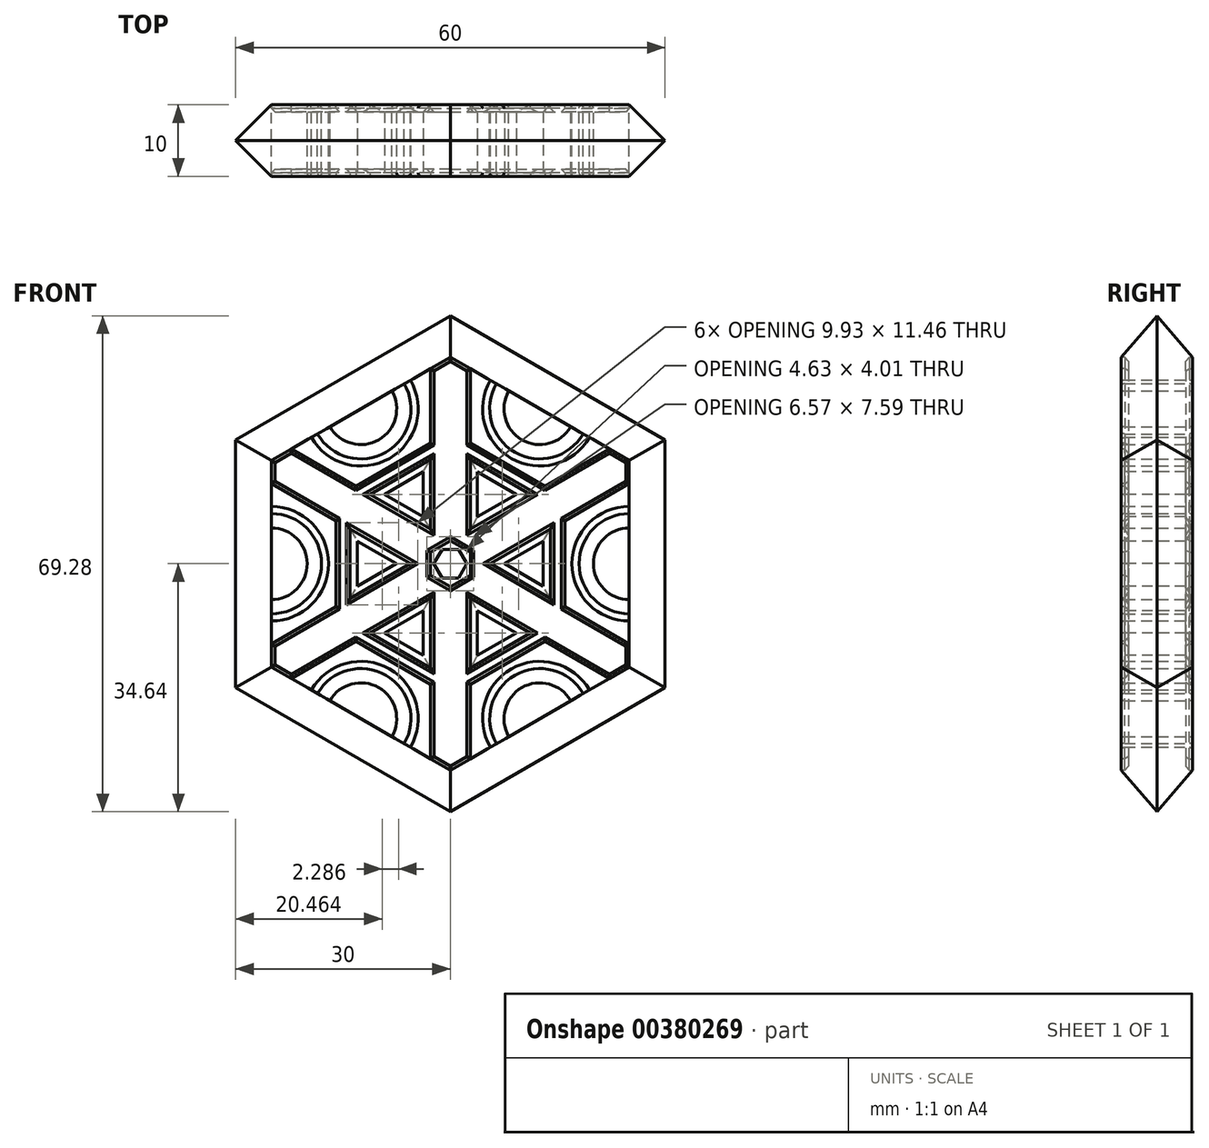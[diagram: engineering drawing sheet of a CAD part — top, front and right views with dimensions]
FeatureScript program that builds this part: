
annotation { "Feature Type Name" : "Feature", "Feature Type Description" : "" }
export const myFeature = defineFeature(function(context is Context, id is Id, definition is map)
    precondition{}
    {
        {
            var Q0;
            Q0=qCreatedBy(makeId("Front.planeOp"),FACE);
            var sketch = newSketch(context, id + "F0", { "sketchPlane" : qUnion([Q0])});
            skCircle(sketch, "E0.cCircle", {"center": v(0, 0) * mm, "radius": 25 * mm, "construction": true});
            skLineSegment(sketch, "E0.0", {"start": v(-25, -14.43) * mm, "end": v(-25, 14.43) * mm});
            skLineSegment(sketch, "E0.1", {"start": v(-25, 14.43) * mm, "end": v(0, 28.87) * mm});
            skLineSegment(sketch, "E0.2", {"start": v(0, 28.87) * mm, "end": v(25, 14.43) * mm});
            skLineSegment(sketch, "E0.3", {"start": v(25, 14.43) * mm, "end": v(25, -14.43) * mm});
            skLineSegment(sketch, "E0.4", {"start": v(25, -14.43) * mm, "end": v(0, -28.87) * mm});
            skLineSegment(sketch, "E0.5", {"start": v(0, -28.87) * mm, "end": v(-25, -14.43) * mm});
            skPoint(sketch, "E0.0.midPoint", {"position": v(-25, 0) * mm});
            skCircle(sketch, "E1", {"center": v(-12.5, 21.65) * mm, "radius": 5 * mm});
            skCircle(sketch, "E2", {"center": v(12.5, 21.65) * mm, "radius": 5 * mm});
            skCircle(sketch, "E3", {"center": v(25, 0) * mm, "radius": 5 * mm});
            skCircle(sketch, "E4", {"center": v(12.5, -21.65) * mm, "radius": 5 * mm});
            skCircle(sketch, "E5", {"center": v(-12.5, -21.65) * mm, "radius": 5 * mm});
            skCircle(sketch, "E6", {"center": v(-25, 0) * mm, "radius": 5 * mm});
            skArc(sketch, "E7", {"start": v(-25, -7) * mm, "mid": v(-18, 0) * mm, "end": v(-25, 7) * mm});
            skArc(sketch, "E8", {"start": v(-6.44, -25.15) * mm, "mid": v(-9, -15.59) * mm, "end": v(-18.56, -18.15) * mm});
            skArc(sketch, "E9", {"start": v(18.56, -18.15) * mm, "mid": v(9, -15.59) * mm, "end": v(6.44, -25.15) * mm});
            skCircle(sketch, "E10.cCircle", {"center": v(0, 0) * mm, "radius": 30 * mm, "construction": true});
            skLineSegment(sketch, "E10.0", {"start": v(-30, -17.32) * mm, "end": v(-30, 17.32) * mm});
            skLineSegment(sketch, "E10.1", {"start": v(-30, 17.32) * mm, "end": v(0, 34.64) * mm});
            skLineSegment(sketch, "E10.2", {"start": v(0, 34.64) * mm, "end": v(30, 17.32) * mm});
            skLineSegment(sketch, "E10.3", {"start": v(30, 17.32) * mm, "end": v(30, -17.32) * mm});
            skLineSegment(sketch, "E10.4", {"start": v(30, -17.32) * mm, "end": v(0, -34.64) * mm});
            skLineSegment(sketch, "E10.5", {"start": v(0, -34.64) * mm, "end": v(-30, -17.32) * mm});
            skPoint(sketch, "E10.0.midPoint", {"position": v(-30, 0) * mm});
            skArc(sketch, "E11", {"start": v(6.44, 25.15) * mm, "mid": v(9, 15.59) * mm, "end": v(18.56, 18.15) * mm});
            skArc(sketch, "E12", {"start": v(25, 7) * mm, "mid": v(18, 0) * mm, "end": v(25, -7) * mm});
            skArc(sketch, "E13", {"start": v(-18.56, 18.15) * mm, "mid": v(-9, 15.59) * mm, "end": v(-6.44, 25.15) * mm});
            skArc(sketch, "E14", {"start": v(-25, -8) * mm, "mid": v(-17, 0) * mm, "end": v(-25, 8) * mm});
            skArc(sketch, "E15", {"start": v(-19.43, 17.65) * mm, "mid": v(-8.5, 14.72) * mm, "end": v(-5.57, 25.65) * mm});
            skArc(sketch, "E16", {"start": v(5.57, 25.65) * mm, "mid": v(8.5, 14.72) * mm, "end": v(19.43, 17.65) * mm});
            skArc(sketch, "E17", {"start": v(25, 8) * mm, "mid": v(17, 0) * mm, "end": v(25, -8) * mm});
            skArc(sketch, "E18", {"start": v(19.43, -17.65) * mm, "mid": v(8.5, -14.72) * mm, "end": v(5.57, -25.65) * mm});
            skArc(sketch, "E19", {"start": v(-5.57, -25.65) * mm, "mid": v(-8.5, -14.72) * mm, "end": v(-19.43, -17.65) * mm});
            skSolve(sketch);
        }
        {
            var Q0;
            {var subQ0=sQuery(id+"F0.wireOp",EDGE,"E6");var subQ1=sQuery(id+"F0.wireOp",EDGE,"E0.0");var subQ2=makeQuery(id+"F0.imprint","INTERSECT",VERTEX,{"disambiguationData":[OD(0.0)],"derivedFrom":[subQ1,subQ0]});Q0=makeQuery(id+"F0.imprint","IMPRINT",FACE,{"disambiguationData":[TD([[makeQuery(id+"F0.imprint","IMPRINT",EDGE,{"disambiguationData":[TD([[subQ2,-1.0]])],"derivedFrom":subQ1}),1.0]])]});}
            var Q1;
            {var subQ0=sQuery(id+"F0.wireOp",EDGE,"E2");var subQ1=sQuery(id+"F0.wireOp",EDGE,"E0.2");var subQ2=makeQuery(id+"F0.imprint","INTERSECT",VERTEX,{"disambiguationData":[OD(0.0)],"derivedFrom":[subQ1,subQ0]});Q1=makeQuery(id+"F0.imprint","IMPRINT",FACE,{"disambiguationData":[TD([[makeQuery(id+"F0.imprint","IMPRINT",EDGE,{"disambiguationData":[TD([[subQ2,-1.0]])],"derivedFrom":subQ1}),1.0]])]});}
            var Q2;
            {var subQ0=sQuery(id+"F0.wireOp",EDGE,"E3");var subQ1=sQuery(id+"F0.wireOp",EDGE,"E0.3");var subQ2=makeQuery(id+"F0.imprint","INTERSECT",VERTEX,{"disambiguationData":[OD(0.0)],"derivedFrom":[subQ1,subQ0]});Q2=makeQuery(id+"F0.imprint","IMPRINT",FACE,{"disambiguationData":[TD([[makeQuery(id+"F0.imprint","IMPRINT",EDGE,{"disambiguationData":[TD([[subQ2,-1.0]])],"derivedFrom":subQ1}),1.0]])]});}
            var Q3;
            {var subQ0=sQuery(id+"F0.wireOp",EDGE,"E4");var subQ1=sQuery(id+"F0.wireOp",EDGE,"E0.4");var subQ2=makeQuery(id+"F0.imprint","INTERSECT",VERTEX,{"disambiguationData":[OD(0.0)],"derivedFrom":[subQ1,subQ0]});Q3=makeQuery(id+"F0.imprint","IMPRINT",FACE,{"disambiguationData":[TD([[makeQuery(id+"F0.imprint","IMPRINT",EDGE,{"disambiguationData":[TD([[subQ2,-1.0]])],"derivedFrom":subQ1}),1.0]])]});}
            var Q4;
            {var subQ0=sQuery(id+"F0.wireOp",EDGE,"E5");var subQ1=sQuery(id+"F0.wireOp",EDGE,"E0.5");var subQ2=makeQuery(id+"F0.imprint","INTERSECT",VERTEX,{"disambiguationData":[OD(0.0)],"derivedFrom":[subQ1,subQ0]});Q4=makeQuery(id+"F0.imprint","IMPRINT",FACE,{"disambiguationData":[TD([[makeQuery(id+"F0.imprint","IMPRINT",EDGE,{"disambiguationData":[TD([[subQ2,-1.0]])],"derivedFrom":subQ1}),1.0]])]});}
            var Q5;
            {var subQ0=sQuery(id+"F0.wireOp",EDGE,"E0.5");var subQ1=sQuery(id+"F0.wireOp",EDGE,"E0.0");var subQ2=makeQuery(id+"F0.imprint","INTERSECT",VERTEX,{"derivedFrom":[subQ1,subQ0]});Q5=makeQuery(id+"F0.imprint","IMPRINT",FACE,{"disambiguationData":[TD([[makeQuery(id+"F0.imprint","IMPRINT",EDGE,{"disambiguationData":[TD([[subQ2,-1.0]])],"derivedFrom":subQ1}),1.0]])]});}
            var Q6;
            {var subQ4=sQuery(id+"F0.wireOp",EDGE,"E0.0");var subQ6=makeQuery(id+"F0.imprint","INTERSECT",VERTEX,{"disambiguationData":[OD(1.0)],"derivedFrom":[subQ4,sQuery(id+"F0.wireOp",EDGE,"E7")]});Q6=makeQuery(id+"F0.imprint","IMPRINT",FACE,{"disambiguationData":[TD([[makeQuery(id+"F0.imprint","IMPRINT",EDGE,{"disambiguationData":[TD([[subQ6,1.0]])],"derivedFrom":subQ4}),1.0]])]});}
            var Q7;
            {var subQ8=sQuery(id+"F0.wireOp",EDGE,"E0.1");var subQ12=makeQuery(id+"F0.imprint","INTERSECT",VERTEX,{"disambiguationData":[OD(1.0)],"derivedFrom":[subQ8,sQuery(id+"F0.wireOp",EDGE,"E13")]});Q7=makeQuery(id+"F0.imprint","IMPRINT",FACE,{"disambiguationData":[TD([[makeQuery(id+"F0.imprint","IMPRINT",EDGE,{"disambiguationData":[TD([[subQ12,1.0]])],"derivedFrom":subQ8}),1.0]])]});}
            var Q8;
            {var subQ4=sQuery(id+"F0.wireOp",EDGE,"E0.2");var subQ6=makeQuery(id+"F0.imprint","INTERSECT",VERTEX,{"disambiguationData":[OD(1.0)],"derivedFrom":[subQ4,sQuery(id+"F0.wireOp",EDGE,"E11")]});Q8=makeQuery(id+"F0.imprint","IMPRINT",FACE,{"disambiguationData":[TD([[makeQuery(id+"F0.imprint","IMPRINT",EDGE,{"disambiguationData":[TD([[subQ6,1.0]])],"derivedFrom":subQ4}),1.0]])]});}
            var Q9;
            {var subQ4=sQuery(id+"F0.wireOp",EDGE,"E0.3");var subQ6=makeQuery(id+"F0.imprint","INTERSECT",VERTEX,{"disambiguationData":[OD(1.0)],"derivedFrom":[subQ4,sQuery(id+"F0.wireOp",EDGE,"E12")]});Q9=makeQuery(id+"F0.imprint","IMPRINT",FACE,{"disambiguationData":[TD([[makeQuery(id+"F0.imprint","IMPRINT",EDGE,{"disambiguationData":[TD([[subQ6,1.0]])],"derivedFrom":subQ4}),1.0]])]});}
            var Q10;
            {var subQ4=sQuery(id+"F0.wireOp",EDGE,"E0.4");var subQ6=makeQuery(id+"F0.imprint","INTERSECT",VERTEX,{"disambiguationData":[OD(1.0)],"derivedFrom":[subQ4,sQuery(id+"F0.wireOp",EDGE,"E9")]});Q10=makeQuery(id+"F0.imprint","IMPRINT",FACE,{"disambiguationData":[TD([[makeQuery(id+"F0.imprint","IMPRINT",EDGE,{"disambiguationData":[TD([[subQ6,1.0]])],"derivedFrom":subQ4}),1.0]])]});}
            var Q11;
            {var subQ0=sQuery(id+"F0.wireOp",EDGE,"E1");var subQ1=sQuery(id+"F0.wireOp",EDGE,"E0.1");var subQ2=makeQuery(id+"F0.imprint","INTERSECT",VERTEX,{"disambiguationData":[OD(0.0)],"derivedFrom":[subQ1,subQ0]});Q11=makeQuery(id+"F0.imprint","IMPRINT",FACE,{"disambiguationData":[TD([[makeQuery(id+"F0.imprint","IMPRINT",EDGE,{"disambiguationData":[TD([[subQ2,-1.0]])],"derivedFrom":subQ1}),1.0]])]});}
            var Q12;
            {var subQ15=sQuery(id+"F0.wireOp",EDGE,"E14");Q12=makeQuery(id+"F0.imprint","IMPRINT",FACE,{"disambiguationData":[TD([[makeQuery(id+"F0.imprint","IMPRINT",EDGE,{"derivedFrom":subQ15}),-1.0]])]});}
            var Q13;
            {var subQ0=sQuery(id+"F0.wireOp",EDGE,"E7");Q13=makeQuery(id+"F0.imprint","IMPRINT",FACE,{"disambiguationData":[TD([[makeQuery(id+"F0.imprint","IMPRINT",EDGE,{"derivedFrom":subQ0}),1.0]])]});}
            var Q14;
            {var subQ0=sQuery(id+"F0.wireOp",EDGE,"E13");Q14=makeQuery(id+"F0.imprint","IMPRINT",FACE,{"disambiguationData":[TD([[makeQuery(id+"F0.imprint","IMPRINT",EDGE,{"derivedFrom":subQ0}),1.0]])]});}
            var Q15;
            {var subQ0=sQuery(id+"F0.wireOp",EDGE,"E11");Q15=makeQuery(id+"F0.imprint","IMPRINT",FACE,{"disambiguationData":[TD([[makeQuery(id+"F0.imprint","IMPRINT",EDGE,{"derivedFrom":subQ0}),1.0]])]});}
            var Q16;
            {var subQ0=sQuery(id+"F0.wireOp",EDGE,"E12");Q16=makeQuery(id+"F0.imprint","IMPRINT",FACE,{"disambiguationData":[TD([[makeQuery(id+"F0.imprint","IMPRINT",EDGE,{"derivedFrom":subQ0}),1.0]])]});}
            var Q17;
            {var subQ0=sQuery(id+"F0.wireOp",EDGE,"E9");Q17=makeQuery(id+"F0.imprint","IMPRINT",FACE,{"disambiguationData":[TD([[makeQuery(id+"F0.imprint","IMPRINT",EDGE,{"derivedFrom":subQ0}),1.0]])]});}
            var Q18;
            {var subQ0=sQuery(id+"F0.wireOp",EDGE,"E8");Q18=makeQuery(id+"F0.imprint","IMPRINT",FACE,{"disambiguationData":[TD([[makeQuery(id+"F0.imprint","IMPRINT",EDGE,{"derivedFrom":subQ0}),1.0]])]});}
            extrude(context, id + "F1", {"entities" : qUnion([Q0, Q1, Q2, Q3, Q4, Q5, Q6, Q7, Q8, Q9, Q10, Q11, Q12, Q13, Q14, Q15, Q16, Q17, Q18]), "depth" : 10 * mm});
        }
        {
            var Q0;
            Q0=makeQuery(id+"F1.opExtrude","CAP_EDGE",EDGE,{"disambiguationData":[OSD([sQuery(id+"F0.wireOp",EDGE,"E10.0")])],"isStart":false});
            var Q1;
            Q1=makeQuery(id+"F1.opExtrude","CAP_EDGE",EDGE,{"disambiguationData":[OSD([sQuery(id+"F0.wireOp",EDGE,"E10.1")])],"isStart":false});
            var Q2;
            Q2=makeQuery(id+"F1.opExtrude","CAP_EDGE",EDGE,{"disambiguationData":[OSD([sQuery(id+"F0.wireOp",EDGE,"E10.2")])],"isStart":false});
            var Q3;
            Q3=makeQuery(id+"F1.opExtrude","CAP_EDGE",EDGE,{"disambiguationData":[OSD([sQuery(id+"F0.wireOp",EDGE,"E10.3")])],"isStart":false});
            var Q4;
            Q4=makeQuery(id+"F1.opExtrude","CAP_EDGE",EDGE,{"disambiguationData":[OSD([sQuery(id+"F0.wireOp",EDGE,"E10.4")])],"isStart":false});
            var Q5;
            Q5=makeQuery(id+"F1.opExtrude","CAP_EDGE",EDGE,{"disambiguationData":[OSD([sQuery(id+"F0.wireOp",EDGE,"E10.5")])],"isStart":false});
            var Q6;
            Q6=makeQuery(id+"F1.opExtrude","CAP_EDGE",EDGE,{"disambiguationData":[OSD([sQuery(id+"F0.wireOp",EDGE,"E10.3")])],"isStart":true});
            var Q7;
            Q7=makeQuery(id+"F1.opExtrude","CAP_EDGE",EDGE,{"disambiguationData":[OSD([sQuery(id+"F0.wireOp",EDGE,"E10.2")])],"isStart":true});
            var Q8;
            Q8=makeQuery(id+"F1.opExtrude","CAP_EDGE",EDGE,{"disambiguationData":[OSD([sQuery(id+"F0.wireOp",EDGE,"E10.1")])],"isStart":true});
            var Q9;
            Q9=makeQuery(id+"F1.opExtrude","CAP_EDGE",EDGE,{"disambiguationData":[OSD([sQuery(id+"F0.wireOp",EDGE,"E10.0")])],"isStart":true});
            var Q10;
            Q10=makeQuery(id+"F1.opExtrude","CAP_EDGE",EDGE,{"disambiguationData":[OSD([sQuery(id+"F0.wireOp",EDGE,"E10.5")])],"isStart":true});
            var Q11;
            Q11=makeQuery(id+"F1.opExtrude","CAP_EDGE",EDGE,{"disambiguationData":[OSD([sQuery(id+"F0.wireOp",EDGE,"E10.4")])],"isStart":true});
            chamfer(context, id + "F2", {"entities" : qUnion([Q0, Q1, Q2, Q3, Q4, Q5, Q6, Q7, Q8, Q9, Q10, Q11]), "width" : 5 * mm, "tangentPropagation" : true});
        }
        {
            var Q0;
            Q0=makeQuery(id+"F2.opChamfer","SPLIT",FACE,{"disambiguationData":[OD(6.0)],"derivedFrom":makeQuery(id+"F1.opExtrude","CAP_FACE",FACE,{"disambiguationData":[OSD([sQuery(id+"F0.wireOp",EDGE,"E0.0"),sQuery(id+"F0.wireOp",EDGE,"E0.1"),sQuery(id+"F0.wireOp",EDGE,"E0.2"),sQuery(id+"F0.wireOp",EDGE,"E0.3"),sQuery(id+"F0.wireOp",EDGE,"E0.4"),sQuery(id+"F0.wireOp",EDGE,"E0.5"),sQuery(id+"F0.wireOp",EDGE,"E1"),sQuery(id+"F0.wireOp",EDGE,"E2"),sQuery(id+"F0.wireOp",EDGE,"E3"),sQuery(id+"F0.wireOp",EDGE,"E4"),sQuery(id+"F0.wireOp",EDGE,"E5"),sQuery(id+"F0.wireOp",EDGE,"E6"),sQuery(id+"F0.wireOp",EDGE,"E7"),sQuery(id+"F0.wireOp",EDGE,"E8"),sQuery(id+"F0.wireOp",EDGE,"E9"),sQuery(id+"F0.wireOp",EDGE,"E10.0"),sQuery(id+"F0.wireOp",EDGE,"E10.1"),sQuery(id+"F0.wireOp",EDGE,"E10.2"),sQuery(id+"F0.wireOp",EDGE,"E10.3"),sQuery(id+"F0.wireOp",EDGE,"E10.4"),sQuery(id+"F0.wireOp",EDGE,"E10.5"),sQuery(id+"F0.wireOp",EDGE,"E11"),sQuery(id+"F0.wireOp",EDGE,"E12"),sQuery(id+"F0.wireOp",EDGE,"E13"),sQuery(id+"F0.wireOp",EDGE,"E14"),sQuery(id+"F0.wireOp",EDGE,"E15"),sQuery(id+"F0.wireOp",EDGE,"E16"),sQuery(id+"F0.wireOp",EDGE,"E17"),sQuery(id+"F0.wireOp",EDGE,"E18"),sQuery(id+"F0.wireOp",EDGE,"E19")])],"isStart":false})});
            var sketch = newSketch(context, id + "F3", { "sketchPlane" : qUnion([Q0])});
            skLineSegment(sketch, "E20", {"start": v(-25, -11.22) * mm, "end": v(22.21, 16.04) * mm});
            skLineSegment(sketch, "E21", {"start": v(-22.21, -16.04) * mm, "end": v(25, 11.22) * mm});
            skLineSegment(sketch, "E22", {"start": v(-2.79, 27.26) * mm, "end": v(-2.79, -27.26) * mm});
            skLineSegment(sketch, "E23", {"start": v(2.79, 27.26) * mm, "end": v(2.79, -27.26) * mm});
            skLineSegment(sketch, "E24", {"start": v(-25, 11.22) * mm, "end": v(22.21, -16.04) * mm});
            skLineSegment(sketch, "E25", {"start": v(-22.21, 16.04) * mm, "end": v(25, -11.22) * mm});
            skLineSegment(sketch, "E26", {"start": v(-25, 14.43) * mm, "end": v(-22.21, 16.04) * mm});
            skLineSegment(sketch, "E27", {"start": v(-25, 14.43) * mm, "end": v(-25, 11.22) * mm});
            skLineSegment(sketch, "E28", {"start": v(-2.79, 27.26) * mm, "end": v(0, 28.87) * mm});
            skLineSegment(sketch, "E29", {"start": v(0, 28.87) * mm, "end": v(2.79, 27.26) * mm});
            skLineSegment(sketch, "E30", {"start": v(22.21, 16.04) * mm, "end": v(25, 14.43) * mm});
            skLineSegment(sketch, "E31", {"start": v(25, 14.43) * mm, "end": v(25, 11.22) * mm});
            skLineSegment(sketch, "E32", {"start": v(25, -11.22) * mm, "end": v(25, -14.43) * mm});
            skLineSegment(sketch, "E33", {"start": v(25, -14.43) * mm, "end": v(22.21, -16.04) * mm});
            skLineSegment(sketch, "E34", {"start": v(2.79, -27.26) * mm, "end": v(0, -28.87) * mm});
            skLineSegment(sketch, "E35", {"start": v(0, -28.87) * mm, "end": v(-2.79, -27.26) * mm});
            skLineSegment(sketch, "E36", {"start": v(-22.21, -16.04) * mm, "end": v(-25, -14.43) * mm});
            skLineSegment(sketch, "E37", {"start": v(-25, -14.43) * mm, "end": v(-25, -11.22) * mm});
            skCircle(sketch, "E38.cCircle", {"center": v(0, 0) * mm, "radius": 16 * mm, "construction": true});
            skLineSegment(sketch, "E38.0", {"start": v(-16, -9.24) * mm, "end": v(-16, 9.24) * mm});
            skLineSegment(sketch, "E38.1", {"start": v(-16, 9.24) * mm, "end": v(0, 18.48) * mm});
            skLineSegment(sketch, "E38.2", {"start": v(0, 18.48) * mm, "end": v(16, 9.24) * mm});
            skLineSegment(sketch, "E38.3", {"start": v(16, 9.24) * mm, "end": v(16, -9.24) * mm});
            skLineSegment(sketch, "E38.4", {"start": v(16, -9.24) * mm, "end": v(0, -18.48) * mm});
            skLineSegment(sketch, "E38.5", {"start": v(0, -18.48) * mm, "end": v(-16, -9.24) * mm});
            skPoint(sketch, "E38.0.midPoint", {"position": v(-16, 0) * mm});
            skCircle(sketch, "E39.cCircle", {"center": v(0, 0) * mm, "radius": 14 * mm, "construction": true});
            skPoint(sketch, "E39.cCircle.perimeterSnap0", {"position": v(-2.79, 0) * mm});
            skLineSegment(sketch, "E39.0", {"start": v(-14, -8.08) * mm, "end": v(-14, 8.08) * mm});
            skLineSegment(sketch, "E39.1", {"start": v(-14, 8.08) * mm, "end": v(0, 16.17) * mm});
            skLineSegment(sketch, "E39.2", {"start": v(0, 16.17) * mm, "end": v(14, 8.08) * mm});
            skLineSegment(sketch, "E39.3", {"start": v(14, 8.08) * mm, "end": v(14, -8.08) * mm});
            skLineSegment(sketch, "E39.4", {"start": v(14, -8.08) * mm, "end": v(0, -16.17) * mm});
            skLineSegment(sketch, "E39.5", {"start": v(0, -16.17) * mm, "end": v(-14, -8.08) * mm});
            skPoint(sketch, "E39.0.midPoint", {"position": v(-14, 0) * mm});
            skPoint(sketch, "E39.0.midPoint.positionSnap0", {"position": v(-2.79, 0) * mm});
            skSolve(sketch);
        }
        {
            var Q0;
            {var subQ7=sQuery(id+"F3.wireOp",EDGE,"E36");Q0=makeQuery(id+"F3.imprint","IMPRINT",FACE,{"disambiguationData":[TD([[makeQuery(id+"F3.imprint","IMPRINT",EDGE,{"derivedFrom":subQ7}),1.0]])]});}
            var Q1;
            {var subQ0=sQuery(id+"F3.wireOp",EDGE,"E26");Q1=makeQuery(id+"F3.imprint","IMPRINT",FACE,{"disambiguationData":[TD([[makeQuery(id+"F3.imprint","IMPRINT",EDGE,{"derivedFrom":subQ0}),1.0]])]});}
            var Q2;
            {var subQ11=sQuery(id+"F3.wireOp",EDGE,"E28");Q2=makeQuery(id+"F3.imprint","IMPRINT",FACE,{"disambiguationData":[TD([[makeQuery(id+"F3.imprint","IMPRINT",EDGE,{"derivedFrom":subQ11}),1.0]])]});}
            var Q3;
            {var subQ11=sQuery(id+"F3.wireOp",EDGE,"E30");Q3=makeQuery(id+"F3.imprint","IMPRINT",FACE,{"disambiguationData":[TD([[makeQuery(id+"F3.imprint","IMPRINT",EDGE,{"derivedFrom":subQ11}),1.0]])]});}
            var Q4;
            {var subQ5=sQuery(id+"F3.wireOp",EDGE,"E34");Q4=makeQuery(id+"F3.imprint","IMPRINT",FACE,{"disambiguationData":[TD([[makeQuery(id+"F3.imprint","IMPRINT",EDGE,{"derivedFrom":subQ5}),1.0]])]});}
            var Q5;
            {var subQ0=sQuery(id+"F3.wireOp",EDGE,"E32");Q5=makeQuery(id+"F3.imprint","IMPRINT",FACE,{"disambiguationData":[TD([[makeQuery(id+"F3.imprint","IMPRINT",EDGE,{"derivedFrom":subQ0}),1.0]])]});}
            var Q6;
            {var subQ0=sQuery(id+"F3.wireOp",EDGE,"E22");var subQ1=sQuery(id+"F3.wireOp",EDGE,"E20");var subQ2=makeQuery(id+"F3.imprint","INTERSECT",VERTEX,{"derivedFrom":[subQ1,subQ0]});Q6=makeQuery(id+"F3.imprint","IMPRINT",FACE,{"disambiguationData":[TD([[makeQuery(id+"F3.imprint","IMPRINT",EDGE,{"disambiguationData":[TD([[subQ2,-1.0]])],"derivedFrom":subQ1}),1.0]])]});}
            var Q7;
            {var subQ0=sQuery(id+"F3.wireOp",EDGE,"E25");var subQ1=sQuery(id+"F3.wireOp",EDGE,"E20");var subQ2=makeQuery(id+"F3.imprint","INTERSECT",VERTEX,{"derivedFrom":[subQ1,subQ0]});Q7=makeQuery(id+"F3.imprint","IMPRINT",FACE,{"disambiguationData":[TD([[makeQuery(id+"F3.imprint","IMPRINT",EDGE,{"disambiguationData":[TD([[subQ2,-1.0]])],"derivedFrom":subQ1}),-1.0]])]});}
            var Q8;
            {var subQ0=sQuery(id+"F3.wireOp",EDGE,"E23");var subQ1=sQuery(id+"F3.wireOp",EDGE,"E21");var subQ2=makeQuery(id+"F3.imprint","INTERSECT",VERTEX,{"derivedFrom":[subQ1,subQ0]});Q8=makeQuery(id+"F3.imprint","IMPRINT",FACE,{"disambiguationData":[TD([[makeQuery(id+"F3.imprint","IMPRINT",EDGE,{"disambiguationData":[TD([[subQ2,-1.0]])],"derivedFrom":subQ1}),1.0]])]});}
            var Q9;
            {var subQ0=sQuery(id+"F3.wireOp",EDGE,"E24");var subQ1=sQuery(id+"F3.wireOp",EDGE,"E21");var subQ2=makeQuery(id+"F3.imprint","INTERSECT",VERTEX,{"derivedFrom":[subQ1,subQ0]});Q9=makeQuery(id+"F3.imprint","IMPRINT",FACE,{"disambiguationData":[TD([[makeQuery(id+"F3.imprint","IMPRINT",EDGE,{"disambiguationData":[TD([[subQ2,-1.0]])],"derivedFrom":subQ1}),-1.0]])]});}
            var Q10;
            {var subQ0=sQuery(id+"F3.wireOp",EDGE,"E22");var subQ1=sQuery(id+"F3.wireOp",EDGE,"E21");var subQ2=makeQuery(id+"F3.imprint","INTERSECT",VERTEX,{"derivedFrom":[subQ1,subQ0]});Q10=makeQuery(id+"F3.imprint","IMPRINT",FACE,{"disambiguationData":[TD([[makeQuery(id+"F3.imprint","IMPRINT",EDGE,{"disambiguationData":[TD([[subQ2,-1.0]])],"derivedFrom":subQ1}),1.0]])]});}
            var Q11;
            {var subQ0=sQuery(id+"F3.wireOp",EDGE,"E24");var subQ1=sQuery(id+"F3.wireOp",EDGE,"E20");var subQ2=makeQuery(id+"F3.imprint","INTERSECT",VERTEX,{"derivedFrom":[subQ1,subQ0]});Q11=makeQuery(id+"F3.imprint","IMPRINT",FACE,{"disambiguationData":[TD([[makeQuery(id+"F3.imprint","IMPRINT",EDGE,{"disambiguationData":[TD([[subQ2,-1.0]])],"derivedFrom":subQ1}),-1.0]])]});}
            var Q12;
            {var subQ5=sQuery(id+"F3.wireOp",EDGE,"E24");var subQ6=sQuery(id+"F3.wireOp",EDGE,"E20");var subQ7=makeQuery(id+"F3.imprint","INTERSECT",VERTEX,{"derivedFrom":[subQ6,subQ5]});Q12=makeQuery(id+"F3.imprint","IMPRINT",FACE,{"disambiguationData":[TD([[makeQuery(id+"F3.imprint","IMPRINT",EDGE,{"disambiguationData":[TD([[subQ7,-1.0]])],"derivedFrom":subQ6}),1.0]])]});}
            var Q13;
            {var subQ0=sQuery(id+"F3.wireOp",EDGE,"E25");var subQ1=sQuery(id+"F3.wireOp",EDGE,"E20");var subQ2=makeQuery(id+"F3.imprint","INTERSECT",VERTEX,{"derivedFrom":[subQ1,subQ0]});Q13=makeQuery(id+"F3.imprint","IMPRINT",FACE,{"disambiguationData":[TD([[makeQuery(id+"F3.imprint","IMPRINT",EDGE,{"disambiguationData":[TD([[subQ2,-1.0]])],"derivedFrom":subQ1}),1.0]])]});}
            var Q14;
            {var subQ0=sQuery(id+"F3.wireOp",EDGE,"E38.1");var subQ1=sQuery(id+"F3.wireOp",EDGE,"E22");var subQ2=makeQuery(id+"F3.imprint","INTERSECT",VERTEX,{"derivedFrom":[subQ1,subQ0]});Q14=makeQuery(id+"F3.imprint","IMPRINT",FACE,{"disambiguationData":[TD([[makeQuery(id+"F3.imprint","IMPRINT",EDGE,{"disambiguationData":[TD([[subQ2,-1.0]])],"derivedFrom":subQ1}),-1.0]])]});}
            var Q15;
            {var subQ0=sQuery(id+"F3.wireOp",EDGE,"E39.2");var subQ1=sQuery(id+"F3.wireOp",EDGE,"E20");var subQ2=makeQuery(id+"F3.imprint","INTERSECT",VERTEX,{"derivedFrom":[subQ1,subQ0]});Q15=makeQuery(id+"F3.imprint","IMPRINT",FACE,{"disambiguationData":[TD([[makeQuery(id+"F3.imprint","IMPRINT",EDGE,{"disambiguationData":[TD([[subQ2,-1.0]])],"derivedFrom":subQ1}),1.0]])]});}
            var Q16;
            {var subQ3=sQuery(id+"F3.wireOp",EDGE,"E23");var subQ5=sQuery(id+"F3.wireOp",EDGE,"E20");var subQ6=makeQuery(id+"F3.imprint","INTERSECT",VERTEX,{"derivedFrom":[subQ5,subQ3]});Q16=makeQuery(id+"F3.imprint","IMPRINT",FACE,{"disambiguationData":[TD([[makeQuery(id+"F3.imprint","IMPRINT",EDGE,{"disambiguationData":[TD([[subQ6,-1.0]])],"derivedFrom":subQ5}),-1.0]])]});}
            var Q17;
            {var subQ1=sQuery(id+"F3.wireOp",EDGE,"E21");var subQ8=sQuery(id+"F3.wireOp",EDGE,"E23");var subQ11=makeQuery(id+"F3.imprint","INTERSECT",VERTEX,{"derivedFrom":[subQ1,subQ8]});Q17=makeQuery(id+"F3.imprint","IMPRINT",FACE,{"disambiguationData":[TD([[makeQuery(id+"F3.imprint","IMPRINT",EDGE,{"disambiguationData":[TD([[subQ11,-1.0]])],"derivedFrom":subQ1}),-1.0]])]});}
            var Q18;
            {var subQ1=sQuery(id+"F3.wireOp",EDGE,"E20");var subQ9=sQuery(id+"F3.wireOp",EDGE,"E39.0");var subQ10=makeQuery(id+"F3.imprint","INTERSECT",VERTEX,{"derivedFrom":[subQ1,subQ9]});Q18=makeQuery(id+"F3.imprint","IMPRINT",FACE,{"disambiguationData":[TD([[makeQuery(id+"F3.imprint","IMPRINT",EDGE,{"disambiguationData":[TD([[subQ10,-1.0]])],"derivedFrom":subQ1}),-1.0]])]});}
            var Q19;
            {var subQ1=sQuery(id+"F3.wireOp",EDGE,"E21");var subQ9=sQuery(id+"F3.wireOp",EDGE,"E22");var subQ11=makeQuery(id+"F3.imprint","INTERSECT",VERTEX,{"derivedFrom":[subQ1,subQ9]});Q19=makeQuery(id+"F3.imprint","IMPRINT",FACE,{"disambiguationData":[TD([[makeQuery(id+"F3.imprint","IMPRINT",EDGE,{"disambiguationData":[TD([[subQ11,-1.0]])],"derivedFrom":subQ1}),-1.0]])]});}
            var Q20;
            {var subQ0=sQuery(id+"F3.wireOp",EDGE,"E39.4");var subQ1=sQuery(id+"F3.wireOp",EDGE,"E23");var subQ2=makeQuery(id+"F3.imprint","INTERSECT",VERTEX,{"derivedFrom":[subQ1,subQ0]});Q20=makeQuery(id+"F3.imprint","IMPRINT",FACE,{"disambiguationData":[TD([[makeQuery(id+"F3.imprint","IMPRINT",EDGE,{"disambiguationData":[TD([[subQ2,-1.0]])],"derivedFrom":subQ1}),1.0]])]});}
            var Q21;
            {var subQ0=sQuery(id+"F3.wireOp",EDGE,"E38.5");var subQ1=sQuery(id+"F3.wireOp",EDGE,"E21");var subQ2=makeQuery(id+"F3.imprint","INTERSECT",VERTEX,{"derivedFrom":[subQ1,subQ0]});Q21=makeQuery(id+"F3.imprint","IMPRINT",FACE,{"disambiguationData":[TD([[makeQuery(id+"F3.imprint","IMPRINT",EDGE,{"disambiguationData":[TD([[subQ2,-1.0]])],"derivedFrom":subQ1}),-1.0]])]});}
            var Q22;
            {var subQ3=sQuery(id+"F3.wireOp",EDGE,"E22");var subQ9=sQuery(id+"F3.wireOp",EDGE,"E39.5");var subQ10=makeQuery(id+"F3.imprint","INTERSECT",VERTEX,{"derivedFrom":[subQ3,subQ9]});Q22=makeQuery(id+"F3.imprint","IMPRINT",FACE,{"disambiguationData":[TD([[makeQuery(id+"F3.imprint","IMPRINT",EDGE,{"disambiguationData":[TD([[subQ10,-1.0]])],"derivedFrom":subQ3}),1.0]])]});}
            var Q23;
            {var subQ7=sQuery(id+"F3.wireOp",EDGE,"E39.4");var subQ9=sQuery(id+"F3.wireOp",EDGE,"E24");var subQ10=makeQuery(id+"F3.imprint","INTERSECT",VERTEX,{"derivedFrom":[subQ9,subQ7]});Q23=makeQuery(id+"F3.imprint","IMPRINT",FACE,{"disambiguationData":[TD([[makeQuery(id+"F3.imprint","IMPRINT",EDGE,{"disambiguationData":[TD([[subQ10,-1.0]])],"derivedFrom":subQ9}),1.0]])]});}
            var Q24;
            {var subQ5=sQuery(id+"F3.wireOp",EDGE,"E20");var subQ9=sQuery(id+"F3.wireOp",EDGE,"E39.2");var subQ11=makeQuery(id+"F3.imprint","INTERSECT",VERTEX,{"derivedFrom":[subQ5,subQ9]});Q24=makeQuery(id+"F3.imprint","IMPRINT",FACE,{"disambiguationData":[TD([[makeQuery(id+"F3.imprint","IMPRINT",EDGE,{"disambiguationData":[TD([[subQ11,-1.0]])],"derivedFrom":subQ5}),-1.0]])]});}
            var Q25;
            {var subQ0=sQuery(id+"F3.wireOp",EDGE,"E39.3");var subQ1=sQuery(id+"F3.wireOp",EDGE,"E21");var subQ2=makeQuery(id+"F3.imprint","INTERSECT",VERTEX,{"derivedFrom":[subQ1,subQ0]});Q25=makeQuery(id+"F3.imprint","IMPRINT",FACE,{"disambiguationData":[TD([[makeQuery(id+"F3.imprint","IMPRINT",EDGE,{"disambiguationData":[TD([[subQ2,-1.0]])],"derivedFrom":subQ1}),-1.0]])]});}
            var Q26;
            {var subQ1=sQuery(id+"F3.wireOp",EDGE,"E38.1");var subQ7=sQuery(id+"F3.wireOp",EDGE,"E22");var subQ8=makeQuery(id+"F3.imprint","INTERSECT",VERTEX,{"derivedFrom":[subQ7,subQ1]});Q26=makeQuery(id+"F3.imprint","IMPRINT",FACE,{"disambiguationData":[TD([[makeQuery(id+"F3.imprint","IMPRINT",EDGE,{"disambiguationData":[TD([[subQ8,-1.0]])],"derivedFrom":subQ7}),1.0]])]});}
            var Q27;
            {var subQ1=sQuery(id+"F3.wireOp",EDGE,"E38.0");var subQ5=sQuery(id+"F3.wireOp",EDGE,"E24");var subQ6=makeQuery(id+"F3.imprint","INTERSECT",VERTEX,{"derivedFrom":[subQ5,subQ1]});Q27=makeQuery(id+"F3.imprint","IMPRINT",FACE,{"disambiguationData":[TD([[makeQuery(id+"F3.imprint","IMPRINT",EDGE,{"disambiguationData":[TD([[subQ6,-1.0]])],"derivedFrom":subQ5}),1.0]])]});}
            var Q28;
            {var subQ0=sQuery(id+"F3.wireOp",EDGE,"E38.0");var subQ1=sQuery(id+"F3.wireOp",EDGE,"E20");var subQ2=makeQuery(id+"F3.imprint","INTERSECT",VERTEX,{"derivedFrom":[subQ1,subQ0]});Q28=makeQuery(id+"F3.imprint","IMPRINT",FACE,{"disambiguationData":[TD([[makeQuery(id+"F3.imprint","IMPRINT",EDGE,{"disambiguationData":[TD([[subQ2,-1.0]])],"derivedFrom":subQ1}),1.0]])]});}
            var Q29;
            {var subQ1=sQuery(id+"F3.wireOp",EDGE,"E38.0");var subQ7=sQuery(id+"F3.wireOp",EDGE,"E20");var subQ8=makeQuery(id+"F3.imprint","INTERSECT",VERTEX,{"derivedFrom":[subQ7,subQ1]});Q29=makeQuery(id+"F3.imprint","IMPRINT",FACE,{"disambiguationData":[TD([[makeQuery(id+"F3.imprint","IMPRINT",EDGE,{"disambiguationData":[TD([[subQ8,-1.0]])],"derivedFrom":subQ7}),-1.0]])]});}
            extrude(context, id + "F4", {"entities" : qUnion([Q0, Q1, Q2, Q3, Q4, Q5, Q6, Q7, Q8, Q9, Q10, Q11, Q12, Q13, Q14, Q15, Q16, Q17, Q18, Q19, Q20, Q21, Q22, Q23, Q24, Q25, Q26, Q27, Q28, Q29]), "operationType" : NewBodyOperationType.REMOVE, "oppositeDirection" : true, "depth" : 1 * mm});
        }
        {
            var Q0;
            Q0=makeQuery(id+"F2.opChamfer","SPLIT",FACE,{"disambiguationData":[OD(6.0)],"derivedFrom":makeQuery(id+"F1.opExtrude","CAP_FACE",FACE,{"disambiguationData":[OSD([sQuery(id+"F0.wireOp",EDGE,"E0.0"),sQuery(id+"F0.wireOp",EDGE,"E0.1"),sQuery(id+"F0.wireOp",EDGE,"E0.2"),sQuery(id+"F0.wireOp",EDGE,"E0.3"),sQuery(id+"F0.wireOp",EDGE,"E0.4"),sQuery(id+"F0.wireOp",EDGE,"E0.5"),sQuery(id+"F0.wireOp",EDGE,"E1"),sQuery(id+"F0.wireOp",EDGE,"E2"),sQuery(id+"F0.wireOp",EDGE,"E3"),sQuery(id+"F0.wireOp",EDGE,"E4"),sQuery(id+"F0.wireOp",EDGE,"E5"),sQuery(id+"F0.wireOp",EDGE,"E6"),sQuery(id+"F0.wireOp",EDGE,"E7"),sQuery(id+"F0.wireOp",EDGE,"E8"),sQuery(id+"F0.wireOp",EDGE,"E9"),sQuery(id+"F0.wireOp",EDGE,"E10.0"),sQuery(id+"F0.wireOp",EDGE,"E10.1"),sQuery(id+"F0.wireOp",EDGE,"E10.2"),sQuery(id+"F0.wireOp",EDGE,"E10.3"),sQuery(id+"F0.wireOp",EDGE,"E10.4"),sQuery(id+"F0.wireOp",EDGE,"E10.5"),sQuery(id+"F0.wireOp",EDGE,"E11"),sQuery(id+"F0.wireOp",EDGE,"E12"),sQuery(id+"F0.wireOp",EDGE,"E13"),sQuery(id+"F0.wireOp",EDGE,"E14"),sQuery(id+"F0.wireOp",EDGE,"E15"),sQuery(id+"F0.wireOp",EDGE,"E16"),sQuery(id+"F0.wireOp",EDGE,"E17"),sQuery(id+"F0.wireOp",EDGE,"E18"),sQuery(id+"F0.wireOp",EDGE,"E19")])],"isStart":true})});
            var sketch = newSketch(context, id + "F5", { "sketchPlane" : qUnion([Q0])});
            skLineSegment(sketch, "E40", {"start": v(-25, -11.22) * mm, "end": v(22.21, 16.04) * mm});
            skLineSegment(sketch, "E41", {"start": v(-22.21, -16.04) * mm, "end": v(25, 11.22) * mm});
            skLineSegment(sketch, "E42", {"start": v(-2.79, 27.26) * mm, "end": v(-2.79, -27.26) * mm});
            skLineSegment(sketch, "E43", {"start": v(2.79, 27.26) * mm, "end": v(2.79, -27.26) * mm});
            skLineSegment(sketch, "E44", {"start": v(-25, 11.22) * mm, "end": v(22.21, -16.04) * mm});
            skLineSegment(sketch, "E45", {"start": v(-22.21, 16.04) * mm, "end": v(25, -11.22) * mm});
            skLineSegment(sketch, "E46", {"start": v(-25, 14.43) * mm, "end": v(-22.21, 16.04) * mm});
            skLineSegment(sketch, "E47", {"start": v(-25, 14.43) * mm, "end": v(-25, 11.22) * mm});
            skLineSegment(sketch, "E48", {"start": v(-2.79, 27.26) * mm, "end": v(0, 28.87) * mm});
            skLineSegment(sketch, "E49", {"start": v(0, 28.87) * mm, "end": v(2.79, 27.26) * mm});
            skLineSegment(sketch, "E50", {"start": v(22.21, 16.04) * mm, "end": v(25, 14.43) * mm});
            skLineSegment(sketch, "E51", {"start": v(25, 14.43) * mm, "end": v(25, 11.22) * mm});
            skLineSegment(sketch, "E52", {"start": v(25, -11.22) * mm, "end": v(25, -14.43) * mm});
            skLineSegment(sketch, "E53", {"start": v(25, -14.43) * mm, "end": v(22.21, -16.04) * mm});
            skLineSegment(sketch, "E54", {"start": v(2.79, -27.26) * mm, "end": v(0, -28.87) * mm});
            skLineSegment(sketch, "E55", {"start": v(0, -28.87) * mm, "end": v(-2.79, -27.26) * mm});
            skLineSegment(sketch, "E56", {"start": v(-22.21, -16.04) * mm, "end": v(-25, -14.43) * mm});
            skLineSegment(sketch, "E57", {"start": v(-25, -14.43) * mm, "end": v(-25, -11.22) * mm});
            skCircle(sketch, "E58.cCircle", {"center": v(0, 0) * mm, "radius": 16 * mm, "construction": true});
            skLineSegment(sketch, "E58.0", {"start": v(-16, -9.24) * mm, "end": v(-16, 9.24) * mm});
            skLineSegment(sketch, "E58.1", {"start": v(-16, 9.24) * mm, "end": v(0, 18.48) * mm});
            skLineSegment(sketch, "E58.2", {"start": v(0, 18.48) * mm, "end": v(16, 9.24) * mm});
            skLineSegment(sketch, "E58.3", {"start": v(16, 9.24) * mm, "end": v(16, -9.24) * mm});
            skLineSegment(sketch, "E58.4", {"start": v(16, -9.24) * mm, "end": v(0, -18.48) * mm});
            skLineSegment(sketch, "E58.5", {"start": v(0, -18.48) * mm, "end": v(-16, -9.24) * mm});
            skPoint(sketch, "E58.0.midPoint", {"position": v(-16, 0) * mm});
            skCircle(sketch, "E59.cCircle", {"center": v(0, 0) * mm, "radius": 14 * mm, "construction": true});
            skPoint(sketch, "E59.cCircle.perimeterSnap0", {"position": v(-2.79, 0) * mm});
            skLineSegment(sketch, "E59.0", {"start": v(-14, -8.08) * mm, "end": v(-14, 8.08) * mm});
            skLineSegment(sketch, "E59.1", {"start": v(-14, 8.08) * mm, "end": v(0, 16.17) * mm});
            skLineSegment(sketch, "E59.2", {"start": v(0, 16.17) * mm, "end": v(14, 8.08) * mm});
            skLineSegment(sketch, "E59.3", {"start": v(14, 8.08) * mm, "end": v(14, -8.08) * mm});
            skLineSegment(sketch, "E59.4", {"start": v(14, -8.08) * mm, "end": v(0, -16.17) * mm});
            skLineSegment(sketch, "E59.5", {"start": v(0, -16.17) * mm, "end": v(-14, -8.08) * mm});
            skPoint(sketch, "E59.0.midPoint", {"position": v(-14, 0) * mm});
            skPoint(sketch, "E59.0.midPoint.positionSnap0", {"position": v(-2.79, 0) * mm});
            skSolve(sketch);
        }
        {
            var Q0;
            Q0 = qSketchRegion(id + "F5", true);
            var Q1;
            {var subQ5=sQuery(id+"F5.wireOp",EDGE,"E44");var subQ6=sQuery(id+"F5.wireOp",EDGE,"E40");var subQ7=makeQuery(id+"F5.imprint","INTERSECT",VERTEX,{"derivedFrom":[subQ6,subQ5]});Q1=makeQuery(id+"F5.imprint","IMPRINT",FACE,{"disambiguationData":[TD([[makeQuery(id+"F5.imprint","IMPRINT",EDGE,{"disambiguationData":[TD([[subQ7,-1.0]])],"derivedFrom":subQ6}),1.0]])]});}
            var Q2;
            {var subQ3=sQuery(id+"F5.wireOp",EDGE,"E43");var subQ5=sQuery(id+"F5.wireOp",EDGE,"E40");var subQ6=makeQuery(id+"F5.imprint","INTERSECT",VERTEX,{"derivedFrom":[subQ5,subQ3]});Q2=makeQuery(id+"F5.imprint","IMPRINT",FACE,{"disambiguationData":[TD([[makeQuery(id+"F5.imprint","IMPRINT",EDGE,{"disambiguationData":[TD([[subQ6,-1.0]])],"derivedFrom":subQ5}),-1.0]])]});}
            var Q3;
            {var subQ1=sQuery(id+"F5.wireOp",EDGE,"E41");var subQ8=sQuery(id+"F5.wireOp",EDGE,"E43");var subQ11=makeQuery(id+"F5.imprint","INTERSECT",VERTEX,{"derivedFrom":[subQ1,subQ8]});Q3=makeQuery(id+"F5.imprint","IMPRINT",FACE,{"disambiguationData":[TD([[makeQuery(id+"F5.imprint","IMPRINT",EDGE,{"disambiguationData":[TD([[subQ11,-1.0]])],"derivedFrom":subQ1}),-1.0]])]});}
            var Q4;
            {var subQ1=sQuery(id+"F5.wireOp",EDGE,"E40");var subQ9=sQuery(id+"F5.wireOp",EDGE,"E59.0");var subQ10=makeQuery(id+"F5.imprint","INTERSECT",VERTEX,{"derivedFrom":[subQ1,subQ9]});Q4=makeQuery(id+"F5.imprint","IMPRINT",FACE,{"disambiguationData":[TD([[makeQuery(id+"F5.imprint","IMPRINT",EDGE,{"disambiguationData":[TD([[subQ10,-1.0]])],"derivedFrom":subQ1}),-1.0]])]});}
            var Q5;
            {var subQ1=sQuery(id+"F5.wireOp",EDGE,"E41");var subQ9=sQuery(id+"F5.wireOp",EDGE,"E42");var subQ11=makeQuery(id+"F5.imprint","INTERSECT",VERTEX,{"derivedFrom":[subQ1,subQ9]});Q5=makeQuery(id+"F5.imprint","IMPRINT",FACE,{"disambiguationData":[TD([[makeQuery(id+"F5.imprint","IMPRINT",EDGE,{"disambiguationData":[TD([[subQ11,-1.0]])],"derivedFrom":subQ1}),-1.0]])]});}
            var Q6;
            {var subQ0=sQuery(id+"F5.wireOp",EDGE,"E45");var subQ1=sQuery(id+"F5.wireOp",EDGE,"E40");var subQ2=makeQuery(id+"F5.imprint","INTERSECT",VERTEX,{"derivedFrom":[subQ1,subQ0]});Q6=makeQuery(id+"F5.imprint","IMPRINT",FACE,{"disambiguationData":[TD([[makeQuery(id+"F5.imprint","IMPRINT",EDGE,{"disambiguationData":[TD([[subQ2,-1.0]])],"derivedFrom":subQ1}),1.0]])]});}
            var Q7;
            {var subQ0=sQuery(id+"F5.wireOp",EDGE,"E42");var subQ1=sQuery(id+"F5.wireOp",EDGE,"E40");var subQ2=makeQuery(id+"F5.imprint","INTERSECT",VERTEX,{"derivedFrom":[subQ1,subQ0]});Q7=makeQuery(id+"F5.imprint","IMPRINT",FACE,{"disambiguationData":[TD([[makeQuery(id+"F5.imprint","IMPRINT",EDGE,{"disambiguationData":[TD([[subQ2,-1.0]])],"derivedFrom":subQ1}),1.0]])]});}
            var Q8;
            {var subQ0=sQuery(id+"F5.wireOp",EDGE,"E45");var subQ1=sQuery(id+"F5.wireOp",EDGE,"E40");var subQ2=makeQuery(id+"F5.imprint","INTERSECT",VERTEX,{"derivedFrom":[subQ1,subQ0]});Q8=makeQuery(id+"F5.imprint","IMPRINT",FACE,{"disambiguationData":[TD([[makeQuery(id+"F5.imprint","IMPRINT",EDGE,{"disambiguationData":[TD([[subQ2,-1.0]])],"derivedFrom":subQ1}),-1.0]])]});}
            var Q9;
            {var subQ0=sQuery(id+"F5.wireOp",EDGE,"E43");var subQ1=sQuery(id+"F5.wireOp",EDGE,"E41");var subQ2=makeQuery(id+"F5.imprint","INTERSECT",VERTEX,{"derivedFrom":[subQ1,subQ0]});Q9=makeQuery(id+"F5.imprint","IMPRINT",FACE,{"disambiguationData":[TD([[makeQuery(id+"F5.imprint","IMPRINT",EDGE,{"disambiguationData":[TD([[subQ2,-1.0]])],"derivedFrom":subQ1}),1.0]])]});}
            var Q10;
            {var subQ0=sQuery(id+"F5.wireOp",EDGE,"E44");var subQ1=sQuery(id+"F5.wireOp",EDGE,"E41");var subQ2=makeQuery(id+"F5.imprint","INTERSECT",VERTEX,{"derivedFrom":[subQ1,subQ0]});Q10=makeQuery(id+"F5.imprint","IMPRINT",FACE,{"disambiguationData":[TD([[makeQuery(id+"F5.imprint","IMPRINT",EDGE,{"disambiguationData":[TD([[subQ2,-1.0]])],"derivedFrom":subQ1}),-1.0]])]});}
            var Q11;
            {var subQ0=sQuery(id+"F5.wireOp",EDGE,"E42");var subQ1=sQuery(id+"F5.wireOp",EDGE,"E41");var subQ2=makeQuery(id+"F5.imprint","INTERSECT",VERTEX,{"derivedFrom":[subQ1,subQ0]});Q11=makeQuery(id+"F5.imprint","IMPRINT",FACE,{"disambiguationData":[TD([[makeQuery(id+"F5.imprint","IMPRINT",EDGE,{"disambiguationData":[TD([[subQ2,-1.0]])],"derivedFrom":subQ1}),1.0]])]});}
            var Q12;
            {var subQ0=sQuery(id+"F5.wireOp",EDGE,"E44");var subQ1=sQuery(id+"F5.wireOp",EDGE,"E40");var subQ2=makeQuery(id+"F5.imprint","INTERSECT",VERTEX,{"derivedFrom":[subQ1,subQ0]});Q12=makeQuery(id+"F5.imprint","IMPRINT",FACE,{"disambiguationData":[TD([[makeQuery(id+"F5.imprint","IMPRINT",EDGE,{"disambiguationData":[TD([[subQ2,-1.0]])],"derivedFrom":subQ1}),-1.0]])]});}
            extrude(context, id + "F6", {"entities" : qUnion([Q0, Q1, Q2, Q3, Q4, Q5, Q6, Q7, Q8, Q9, Q10, Q11, Q12]), "operationType" : NewBodyOperationType.REMOVE, "oppositeDirection" : true, "depth" : 1 * mm});
        }
        {
            var Q0;
            Q0=makeQuery(id+"F6.boolean.opBoolean","COPY",FACE,{"derivedFrom":makeQuery(id+"F6.opExtrude","CAP_FACE",FACE,{"disambiguationData":[OSD([sQuery(id+"F5.wireOp",EDGE,"E40"),sQuery(id+"F5.wireOp",EDGE,"E41"),sQuery(id+"F5.wireOp",EDGE,"E42"),sQuery(id+"F5.wireOp",EDGE,"E43"),sQuery(id+"F5.wireOp",EDGE,"E44"),sQuery(id+"F5.wireOp",EDGE,"E45"),sQuery(id+"F5.wireOp",EDGE,"E46"),sQuery(id+"F5.wireOp",EDGE,"E47"),sQuery(id+"F5.wireOp",EDGE,"E48"),sQuery(id+"F5.wireOp",EDGE,"E49"),sQuery(id+"F5.wireOp",EDGE,"E50"),sQuery(id+"F5.wireOp",EDGE,"E51"),sQuery(id+"F5.wireOp",EDGE,"E52"),sQuery(id+"F5.wireOp",EDGE,"E53"),sQuery(id+"F5.wireOp",EDGE,"E54"),sQuery(id+"F5.wireOp",EDGE,"E55"),sQuery(id+"F5.wireOp",EDGE,"E56"),sQuery(id+"F5.wireOp",EDGE,"E57"),sQuery(id+"F5.wireOp",EDGE,"E58.0"),sQuery(id+"F5.wireOp",EDGE,"E58.1"),sQuery(id+"F5.wireOp",EDGE,"E58.2"),sQuery(id+"F5.wireOp",EDGE,"E58.3"),sQuery(id+"F5.wireOp",EDGE,"E58.4"),sQuery(id+"F5.wireOp",EDGE,"E58.5"),sQuery(id+"F5.wireOp",EDGE,"E59.0"),sQuery(id+"F5.wireOp",EDGE,"E59.1"),sQuery(id+"F5.wireOp",EDGE,"E59.2"),sQuery(id+"F5.wireOp",EDGE,"E59.3"),sQuery(id+"F5.wireOp",EDGE,"E59.4"),sQuery(id+"F5.wireOp",EDGE,"E59.5")])],"isStart":false})});
            var Q1;
            Q1=makeQuery(id+"F4.boolean.opBoolean","COPY",FACE,{"derivedFrom":makeQuery(id+"F4.opExtrude","CAP_FACE",FACE,{"disambiguationData":[OSD([sQuery(id+"F3.wireOp",EDGE,"E20"),sQuery(id+"F3.wireOp",EDGE,"E21"),sQuery(id+"F3.wireOp",EDGE,"E22"),sQuery(id+"F3.wireOp",EDGE,"E23"),sQuery(id+"F3.wireOp",EDGE,"E24"),sQuery(id+"F3.wireOp",EDGE,"E25"),sQuery(id+"F3.wireOp",EDGE,"E26"),sQuery(id+"F3.wireOp",EDGE,"E27"),sQuery(id+"F3.wireOp",EDGE,"E28"),sQuery(id+"F3.wireOp",EDGE,"E29"),sQuery(id+"F3.wireOp",EDGE,"E30"),sQuery(id+"F3.wireOp",EDGE,"E31"),sQuery(id+"F3.wireOp",EDGE,"E32"),sQuery(id+"F3.wireOp",EDGE,"E33"),sQuery(id+"F3.wireOp",EDGE,"E34"),sQuery(id+"F3.wireOp",EDGE,"E35"),sQuery(id+"F3.wireOp",EDGE,"E36"),sQuery(id+"F3.wireOp",EDGE,"E37"),sQuery(id+"F3.wireOp",EDGE,"E38.0"),sQuery(id+"F3.wireOp",EDGE,"E38.1"),sQuery(id+"F3.wireOp",EDGE,"E38.2"),sQuery(id+"F3.wireOp",EDGE,"E38.3"),sQuery(id+"F3.wireOp",EDGE,"E38.4"),sQuery(id+"F3.wireOp",EDGE,"E38.5"),sQuery(id+"F3.wireOp",EDGE,"E39.0"),sQuery(id+"F3.wireOp",EDGE,"E39.1"),sQuery(id+"F3.wireOp",EDGE,"E39.2"),sQuery(id+"F3.wireOp",EDGE,"E39.3"),sQuery(id+"F3.wireOp",EDGE,"E39.4"),sQuery(id+"F3.wireOp",EDGE,"E39.5")])],"isStart":false})});
            chamfer(context, id + "F7", {"entities" : qUnion([Q0, Q1]), "width" : .5 * mm, "tangentPropagation" : true});
        }
        {
            var Q0;
            {var subQ5=sQuery(id+"F5.wireOp",EDGE,"E42");var subQ6=sQuery(id+"F5.wireOp",EDGE,"E40");var subQ7=makeQuery(id+"F5.imprint","INTERSECT",VERTEX,{"derivedFrom":[subQ6,subQ5]});Q0=makeQuery(id+"F6.boolean.opBoolean","SPLIT",FACE,{"disambiguationData":[TD([makeQuery(id+"F6.opExtrude","SWEPT_FACE",FACE,{"disambiguationData":[OSD([subQ6]),TDD([makeQuery(id+"F5.imprint","IMPRINT",EDGE,{"disambiguationData":[TD([[subQ7,-1.0]])],"derivedFrom":subQ6})])]})])],"derivedFrom":makeQuery(id+"F2.opChamfer","SPLIT",FACE,{"disambiguationData":[OD(6.0)],"derivedFrom":makeQuery(id+"F1.opExtrude","CAP_FACE",FACE,{"disambiguationData":[OSD([sQuery(id+"F0.wireOp",EDGE,"E0.0"),sQuery(id+"F0.wireOp",EDGE,"E0.1"),sQuery(id+"F0.wireOp",EDGE,"E0.2"),sQuery(id+"F0.wireOp",EDGE,"E0.3"),sQuery(id+"F0.wireOp",EDGE,"E0.4"),sQuery(id+"F0.wireOp",EDGE,"E0.5"),sQuery(id+"F0.wireOp",EDGE,"E1"),sQuery(id+"F0.wireOp",EDGE,"E2"),sQuery(id+"F0.wireOp",EDGE,"E3"),sQuery(id+"F0.wireOp",EDGE,"E4"),sQuery(id+"F0.wireOp",EDGE,"E5"),sQuery(id+"F0.wireOp",EDGE,"E6"),sQuery(id+"F0.wireOp",EDGE,"E7"),sQuery(id+"F0.wireOp",EDGE,"E8"),sQuery(id+"F0.wireOp",EDGE,"E9"),sQuery(id+"F0.wireOp",EDGE,"E10.0"),sQuery(id+"F0.wireOp",EDGE,"E10.1"),sQuery(id+"F0.wireOp",EDGE,"E10.2"),sQuery(id+"F0.wireOp",EDGE,"E10.3"),sQuery(id+"F0.wireOp",EDGE,"E10.4"),sQuery(id+"F0.wireOp",EDGE,"E10.5"),sQuery(id+"F0.wireOp",EDGE,"E11"),sQuery(id+"F0.wireOp",EDGE,"E12"),sQuery(id+"F0.wireOp",EDGE,"E13"),sQuery(id+"F0.wireOp",EDGE,"E14"),sQuery(id+"F0.wireOp",EDGE,"E15"),sQuery(id+"F0.wireOp",EDGE,"E16"),sQuery(id+"F0.wireOp",EDGE,"E17"),sQuery(id+"F0.wireOp",EDGE,"E18"),sQuery(id+"F0.wireOp",EDGE,"E19")])],"isStart":true})})});}
            var sketch = newSketch(context, id + "F8", { "sketchPlane" : qUnion([Q0])});
            skCircle(sketch, "E60.cCircle", {"center": v(0, 0) * mm, "radius": 2 * mm, "construction": true});
            skLineSegment(sketch, "E60.0", {"start": v(1.16, -2) * mm, "end": v(-1.16, -2) * mm});
            skLineSegment(sketch, "E60.1", {"start": v(-1.16, -2) * mm, "end": v(-2.32, 0) * mm});
            skLineSegment(sketch, "E60.2", {"start": v(-2.32, 0) * mm, "end": v(-1.16, 2) * mm});
            skLineSegment(sketch, "E60.3", {"start": v(-1.16, 2) * mm, "end": v(1.16, 2) * mm});
            skLineSegment(sketch, "E60.4", {"start": v(1.16, 2) * mm, "end": v(2.32, 0) * mm});
            skLineSegment(sketch, "E60.5", {"start": v(2.32, 0) * mm, "end": v(1.16, -2) * mm});
            skPoint(sketch, "E60.0.midPoint", {"position": v(0, -2) * mm});
            skSolve(sketch);
        }
        {
            var Q0;
            Q0 = qSketchRegion(id + "F8", true);
            extrude(context, id + "F9", {"entities" : qUnion([Q0]), "operationType" : NewBodyOperationType.REMOVE, "oppositeDirection" : true, "depth" : 54.3 * mm});
        }
        {
            var Q0;
            Q0=makeQuery(id+"F1.opExtrude","CAP_EDGE",EDGE,{"disambiguationData":[OSD([sQuery(id+"F0.wireOp",EDGE,"E11")])],"isStart":false});
            var Q1;
            Q1=makeQuery(id+"F1.opExtrude","CAP_EDGE",EDGE,{"disambiguationData":[OSD([sQuery(id+"F0.wireOp",EDGE,"E16")])],"isStart":false});
            var Q2;
            Q2=makeQuery(id+"F1.opExtrude","CAP_EDGE",EDGE,{"disambiguationData":[OSD([sQuery(id+"F0.wireOp",EDGE,"E13")])],"isStart":false});
            var Q3;
            Q3=makeQuery(id+"F1.opExtrude","CAP_EDGE",EDGE,{"disambiguationData":[OSD([sQuery(id+"F0.wireOp",EDGE,"E15")])],"isStart":false});
            var Q4;
            Q4=makeQuery(id+"F1.opExtrude","CAP_EDGE",EDGE,{"disambiguationData":[OSD([sQuery(id+"F0.wireOp",EDGE,"E1")])],"isStart":false});
            var Q5;
            Q5=makeQuery(id+"F1.opExtrude","CAP_EDGE",EDGE,{"disambiguationData":[OSD([sQuery(id+"F0.wireOp",EDGE,"E2")])],"isStart":false});
            var Q6;
            Q6=makeQuery(id+"F1.opExtrude","CAP_EDGE",EDGE,{"disambiguationData":[OSD([sQuery(id+"F0.wireOp",EDGE,"E3")])],"isStart":false});
            var Q7;
            Q7=makeQuery(id+"F1.opExtrude","CAP_EDGE",EDGE,{"disambiguationData":[OSD([sQuery(id+"F0.wireOp",EDGE,"E12")])],"isStart":false});
            var Q8;
            Q8=makeQuery(id+"F1.opExtrude","CAP_EDGE",EDGE,{"disambiguationData":[OSD([sQuery(id+"F0.wireOp",EDGE,"E17")])],"isStart":false});
            var Q9;
            Q9=makeQuery(id+"F1.opExtrude","CAP_EDGE",EDGE,{"disambiguationData":[OSD([sQuery(id+"F0.wireOp",EDGE,"E18")])],"isStart":false});
            var Q10;
            Q10=makeQuery(id+"F1.opExtrude","CAP_EDGE",EDGE,{"disambiguationData":[OSD([sQuery(id+"F0.wireOp",EDGE,"E9")])],"isStart":false});
            var Q11;
            Q11=makeQuery(id+"F1.opExtrude","CAP_EDGE",EDGE,{"disambiguationData":[OSD([sQuery(id+"F0.wireOp",EDGE,"E4")])],"isStart":false});
            var Q12;
            Q12=makeQuery(id+"F1.opExtrude","CAP_EDGE",EDGE,{"disambiguationData":[OSD([sQuery(id+"F0.wireOp",EDGE,"E19")])],"isStart":false});
            var Q13;
            Q13=makeQuery(id+"F1.opExtrude","CAP_EDGE",EDGE,{"disambiguationData":[OSD([sQuery(id+"F0.wireOp",EDGE,"E8")])],"isStart":false});
            var Q14;
            Q14=makeQuery(id+"F1.opExtrude","CAP_EDGE",EDGE,{"disambiguationData":[OSD([sQuery(id+"F0.wireOp",EDGE,"E5")])],"isStart":false});
            var Q15;
            Q15=makeQuery(id+"F1.opExtrude","CAP_EDGE",EDGE,{"disambiguationData":[OSD([sQuery(id+"F0.wireOp",EDGE,"E14")])],"isStart":false});
            var Q16;
            Q16=makeQuery(id+"F1.opExtrude","CAP_EDGE",EDGE,{"disambiguationData":[OSD([sQuery(id+"F0.wireOp",EDGE,"E7")])],"isStart":false});
            var Q17;
            Q17=makeQuery(id+"F1.opExtrude","CAP_EDGE",EDGE,{"disambiguationData":[OSD([sQuery(id+"F0.wireOp",EDGE,"E6")])],"isStart":false});
            var Q18;
            Q18=makeQuery(id+"F1.opExtrude","CAP_EDGE",EDGE,{"disambiguationData":[OSD([sQuery(id+"F0.wireOp",EDGE,"E13")])],"isStart":true});
            var Q19;
            Q19=makeQuery(id+"F1.opExtrude","CAP_EDGE",EDGE,{"disambiguationData":[OSD([sQuery(id+"F0.wireOp",EDGE,"E1")])],"isStart":true});
            var Q20;
            Q20=makeQuery(id+"F1.opExtrude","CAP_EDGE",EDGE,{"disambiguationData":[OSD([sQuery(id+"F0.wireOp",EDGE,"E15")])],"isStart":true});
            var Q21;
            Q21=makeQuery(id+"F1.opExtrude","CAP_EDGE",EDGE,{"disambiguationData":[OSD([sQuery(id+"F0.wireOp",EDGE,"E7")])],"isStart":true});
            var Q22;
            Q22=makeQuery(id+"F1.opExtrude","CAP_EDGE",EDGE,{"disambiguationData":[OSD([sQuery(id+"F0.wireOp",EDGE,"E6")])],"isStart":true});
            var Q23;
            Q23=makeQuery(id+"F1.opExtrude","CAP_EDGE",EDGE,{"disambiguationData":[OSD([sQuery(id+"F0.wireOp",EDGE,"E14")])],"isStart":true});
            var Q24;
            Q24=makeQuery(id+"F1.opExtrude","CAP_EDGE",EDGE,{"disambiguationData":[OSD([sQuery(id+"F0.wireOp",EDGE,"E16")])],"isStart":true});
            var Q25;
            Q25=makeQuery(id+"F1.opExtrude","CAP_EDGE",EDGE,{"disambiguationData":[OSD([sQuery(id+"F0.wireOp",EDGE,"E11")])],"isStart":true});
            var Q26;
            Q26=makeQuery(id+"F1.opExtrude","CAP_EDGE",EDGE,{"disambiguationData":[OSD([sQuery(id+"F0.wireOp",EDGE,"E2")])],"isStart":true});
            var Q27;
            Q27=makeQuery(id+"F1.opExtrude","CAP_EDGE",EDGE,{"disambiguationData":[OSD([sQuery(id+"F0.wireOp",EDGE,"E17")])],"isStart":true});
            var Q28;
            Q28=makeQuery(id+"F1.opExtrude","CAP_EDGE",EDGE,{"disambiguationData":[OSD([sQuery(id+"F0.wireOp",EDGE,"E12")])],"isStart":true});
            var Q29;
            Q29=makeQuery(id+"F1.opExtrude","CAP_EDGE",EDGE,{"disambiguationData":[OSD([sQuery(id+"F0.wireOp",EDGE,"E3")])],"isStart":true});
            var Q30;
            Q30=makeQuery(id+"F1.opExtrude","CAP_EDGE",EDGE,{"disambiguationData":[OSD([sQuery(id+"F0.wireOp",EDGE,"E4")])],"isStart":true});
            var Q31;
            Q31=makeQuery(id+"F1.opExtrude","CAP_EDGE",EDGE,{"disambiguationData":[OSD([sQuery(id+"F0.wireOp",EDGE,"E9")])],"isStart":true});
            var Q32;
            Q32=makeQuery(id+"F1.opExtrude","CAP_EDGE",EDGE,{"disambiguationData":[OSD([sQuery(id+"F0.wireOp",EDGE,"E18")])],"isStart":true});
            var Q33;
            Q33=makeQuery(id+"F1.opExtrude","CAP_EDGE",EDGE,{"disambiguationData":[OSD([sQuery(id+"F0.wireOp",EDGE,"E19")])],"isStart":true});
            var Q34;
            Q34=makeQuery(id+"F1.opExtrude","CAP_EDGE",EDGE,{"disambiguationData":[OSD([sQuery(id+"F0.wireOp",EDGE,"E8")])],"isStart":true});
            var Q35;
            Q35=makeQuery(id+"F1.opExtrude","CAP_EDGE",EDGE,{"disambiguationData":[OSD([sQuery(id+"F0.wireOp",EDGE,"E5")])],"isStart":true});
            fillet(context, id + "F10", {"entities" : qUnion([Q0, Q1, Q2, Q3, Q4, Q5, Q6, Q7, Q8, Q9, Q10, Q11, Q12, Q13, Q14, Q15, Q16, Q17, Q18, Q19, Q20, Q21, Q22, Q23, Q24, Q25, Q26, Q27, Q28, Q29, Q30, Q31, Q32, Q33, Q34, Q35]), "radius" : .5 * mm, "tangentPropagation" : true, "allowEdgeOverflow" : false});
        }
        {
            var Q0;
            {var subQ0=sQuery(id+"F3.wireOp",EDGE,"E39.1");Q0=makeQuery(id+"F4.boolean.opBoolean","SPLIT",FACE,{"disambiguationData":[TD([makeQuery(id+"F4.opExtrude","SWEPT_FACE",FACE,{"disambiguationData":[OSD([subQ0])]})])],"derivedFrom":makeQuery(id+"F2.opChamfer","SPLIT",FACE,{"disambiguationData":[OD(6.0)],"derivedFrom":makeQuery(id+"F1.opExtrude","CAP_FACE",FACE,{"disambiguationData":[OSD([sQuery(id+"F0.wireOp",EDGE,"E0.0"),sQuery(id+"F0.wireOp",EDGE,"E0.1"),sQuery(id+"F0.wireOp",EDGE,"E0.2"),sQuery(id+"F0.wireOp",EDGE,"E0.3"),sQuery(id+"F0.wireOp",EDGE,"E0.4"),sQuery(id+"F0.wireOp",EDGE,"E0.5"),sQuery(id+"F0.wireOp",EDGE,"E1"),sQuery(id+"F0.wireOp",EDGE,"E2"),sQuery(id+"F0.wireOp",EDGE,"E3"),sQuery(id+"F0.wireOp",EDGE,"E4"),sQuery(id+"F0.wireOp",EDGE,"E5"),sQuery(id+"F0.wireOp",EDGE,"E6"),sQuery(id+"F0.wireOp",EDGE,"E7"),sQuery(id+"F0.wireOp",EDGE,"E8"),sQuery(id+"F0.wireOp",EDGE,"E9"),sQuery(id+"F0.wireOp",EDGE,"E10.0"),sQuery(id+"F0.wireOp",EDGE,"E10.1"),sQuery(id+"F0.wireOp",EDGE,"E10.2"),sQuery(id+"F0.wireOp",EDGE,"E10.3"),sQuery(id+"F0.wireOp",EDGE,"E10.4"),sQuery(id+"F0.wireOp",EDGE,"E10.5"),sQuery(id+"F0.wireOp",EDGE,"E11"),sQuery(id+"F0.wireOp",EDGE,"E12"),sQuery(id+"F0.wireOp",EDGE,"E13"),sQuery(id+"F0.wireOp",EDGE,"E14"),sQuery(id+"F0.wireOp",EDGE,"E15"),sQuery(id+"F0.wireOp",EDGE,"E16"),sQuery(id+"F0.wireOp",EDGE,"E17"),sQuery(id+"F0.wireOp",EDGE,"E18"),sQuery(id+"F0.wireOp",EDGE,"E19")])],"isStart":false})})});}
            var sketch = newSketch(context, id + "F11", { "sketchPlane" : qUnion([Q0])});
            skLineSegment(sketch, "E61", {"start": v(-9.21, 9.7) * mm, "end": v(-3.79, 12.83) * mm});
            skLineSegment(sketch, "E62", {"start": v(-3.79, 12.83) * mm, "end": v(-3.79, 6.56) * mm});
            skLineSegment(sketch, "E63", {"start": v(-3.79, 6.56) * mm, "end": v(-9.21, 9.7) * mm});
            skSolve(sketch);
        }
        {
            var Q0;
            Q0 = qSketchRegion(id + "F11", true);
            extrude(context, id + "F12", {"entities" : qUnion([Q0]), "operationType" : NewBodyOperationType.REMOVE, "oppositeDirection" : true, "depth" : 25 * mm});
        }
        {
            var Q0;
            {var subQ3=sQuery(id+"F3.wireOp",EDGE,"E39.2");Q0=makeQuery(id+"F4.boolean.opBoolean","SPLIT",FACE,{"disambiguationData":[TD([makeQuery(id+"F4.opExtrude","SWEPT_FACE",FACE,{"disambiguationData":[OSD([subQ3])]})])],"derivedFrom":makeQuery(id+"F2.opChamfer","SPLIT",FACE,{"disambiguationData":[OD(6.0)],"derivedFrom":makeQuery(id+"F1.opExtrude","CAP_FACE",FACE,{"disambiguationData":[OSD([sQuery(id+"F0.wireOp",EDGE,"E0.0"),sQuery(id+"F0.wireOp",EDGE,"E0.1"),sQuery(id+"F0.wireOp",EDGE,"E0.2"),sQuery(id+"F0.wireOp",EDGE,"E0.3"),sQuery(id+"F0.wireOp",EDGE,"E0.4"),sQuery(id+"F0.wireOp",EDGE,"E0.5"),sQuery(id+"F0.wireOp",EDGE,"E1"),sQuery(id+"F0.wireOp",EDGE,"E2"),sQuery(id+"F0.wireOp",EDGE,"E3"),sQuery(id+"F0.wireOp",EDGE,"E4"),sQuery(id+"F0.wireOp",EDGE,"E5"),sQuery(id+"F0.wireOp",EDGE,"E6"),sQuery(id+"F0.wireOp",EDGE,"E7"),sQuery(id+"F0.wireOp",EDGE,"E8"),sQuery(id+"F0.wireOp",EDGE,"E9"),sQuery(id+"F0.wireOp",EDGE,"E10.0"),sQuery(id+"F0.wireOp",EDGE,"E10.1"),sQuery(id+"F0.wireOp",EDGE,"E10.2"),sQuery(id+"F0.wireOp",EDGE,"E10.3"),sQuery(id+"F0.wireOp",EDGE,"E10.4"),sQuery(id+"F0.wireOp",EDGE,"E10.5"),sQuery(id+"F0.wireOp",EDGE,"E11"),sQuery(id+"F0.wireOp",EDGE,"E12"),sQuery(id+"F0.wireOp",EDGE,"E13"),sQuery(id+"F0.wireOp",EDGE,"E14"),sQuery(id+"F0.wireOp",EDGE,"E15"),sQuery(id+"F0.wireOp",EDGE,"E16"),sQuery(id+"F0.wireOp",EDGE,"E17"),sQuery(id+"F0.wireOp",EDGE,"E18"),sQuery(id+"F0.wireOp",EDGE,"E19")])],"isStart":false})})});}
            var sketch = newSketch(context, id + "F13", { "sketchPlane" : qUnion([Q0])});
            skLineSegment(sketch, "E64", {"start": v(9.21, 9.7) * mm, "end": v(3.79, 12.83) * mm});
            skLineSegment(sketch, "E65", {"start": v(3.79, 12.83) * mm, "end": v(3.79, 6.56) * mm});
            skLineSegment(sketch, "E66", {"start": v(3.79, 6.56) * mm, "end": v(9.21, 9.7) * mm});
            skSolve(sketch);
        }
        {
            var Q0;
            Q0 = qSketchRegion(id + "F13", true);
            extrude(context, id + "F14", {"entities" : qUnion([Q0]), "operationType" : NewBodyOperationType.REMOVE, "oppositeDirection" : true, "depth" : 25 * mm});
        }
        {
            var Q0;
            {var subQ0=sQuery(id+"F3.wireOp",EDGE,"E39.0");Q0=makeQuery(id+"F4.boolean.opBoolean","SPLIT",FACE,{"disambiguationData":[TD([makeQuery(id+"F4.opExtrude","SWEPT_FACE",FACE,{"disambiguationData":[OSD([subQ0])]})])],"derivedFrom":makeQuery(id+"F2.opChamfer","SPLIT",FACE,{"disambiguationData":[OD(6.0)],"derivedFrom":makeQuery(id+"F1.opExtrude","CAP_FACE",FACE,{"disambiguationData":[OSD([sQuery(id+"F0.wireOp",EDGE,"E0.0"),sQuery(id+"F0.wireOp",EDGE,"E0.1"),sQuery(id+"F0.wireOp",EDGE,"E0.2"),sQuery(id+"F0.wireOp",EDGE,"E0.3"),sQuery(id+"F0.wireOp",EDGE,"E0.4"),sQuery(id+"F0.wireOp",EDGE,"E0.5"),sQuery(id+"F0.wireOp",EDGE,"E1"),sQuery(id+"F0.wireOp",EDGE,"E2"),sQuery(id+"F0.wireOp",EDGE,"E3"),sQuery(id+"F0.wireOp",EDGE,"E4"),sQuery(id+"F0.wireOp",EDGE,"E5"),sQuery(id+"F0.wireOp",EDGE,"E6"),sQuery(id+"F0.wireOp",EDGE,"E7"),sQuery(id+"F0.wireOp",EDGE,"E8"),sQuery(id+"F0.wireOp",EDGE,"E9"),sQuery(id+"F0.wireOp",EDGE,"E10.0"),sQuery(id+"F0.wireOp",EDGE,"E10.1"),sQuery(id+"F0.wireOp",EDGE,"E10.2"),sQuery(id+"F0.wireOp",EDGE,"E10.3"),sQuery(id+"F0.wireOp",EDGE,"E10.4"),sQuery(id+"F0.wireOp",EDGE,"E10.5"),sQuery(id+"F0.wireOp",EDGE,"E11"),sQuery(id+"F0.wireOp",EDGE,"E12"),sQuery(id+"F0.wireOp",EDGE,"E13"),sQuery(id+"F0.wireOp",EDGE,"E14"),sQuery(id+"F0.wireOp",EDGE,"E15"),sQuery(id+"F0.wireOp",EDGE,"E16"),sQuery(id+"F0.wireOp",EDGE,"E17"),sQuery(id+"F0.wireOp",EDGE,"E18"),sQuery(id+"F0.wireOp",EDGE,"E19")])],"isStart":false})})});}
            var sketch = newSketch(context, id + "F15", { "sketchPlane" : qUnion([Q0])});
            skLineSegment(sketch, "E67", {"start": v(-7.57, 0) * mm, "end": v(-13, 3.13) * mm});
            skLineSegment(sketch, "E68", {"start": v(-13, 3.13) * mm, "end": v(-13, -3.13) * mm});
            skLineSegment(sketch, "E69", {"start": v(-7.57, 0) * mm, "end": v(-13, -3.13) * mm});
            skSolve(sketch);
        }
        {
            var Q0;
            Q0 = qSketchRegion(id + "F15", true);
            extrude(context, id + "F16", {"entities" : qUnion([Q0]), "operationType" : NewBodyOperationType.REMOVE, "oppositeDirection" : true, "depth" : 25 * mm});
        }
        {
            var Q0;
            {var subQ3=sQuery(id+"F3.wireOp",EDGE,"E39.3");Q0=makeQuery(id+"F4.boolean.opBoolean","SPLIT",FACE,{"disambiguationData":[TD([makeQuery(id+"F4.opExtrude","SWEPT_FACE",FACE,{"disambiguationData":[OSD([subQ3])]})])],"derivedFrom":makeQuery(id+"F2.opChamfer","SPLIT",FACE,{"disambiguationData":[OD(6.0)],"derivedFrom":makeQuery(id+"F1.opExtrude","CAP_FACE",FACE,{"disambiguationData":[OSD([sQuery(id+"F0.wireOp",EDGE,"E0.0"),sQuery(id+"F0.wireOp",EDGE,"E0.1"),sQuery(id+"F0.wireOp",EDGE,"E0.2"),sQuery(id+"F0.wireOp",EDGE,"E0.3"),sQuery(id+"F0.wireOp",EDGE,"E0.4"),sQuery(id+"F0.wireOp",EDGE,"E0.5"),sQuery(id+"F0.wireOp",EDGE,"E1"),sQuery(id+"F0.wireOp",EDGE,"E2"),sQuery(id+"F0.wireOp",EDGE,"E3"),sQuery(id+"F0.wireOp",EDGE,"E4"),sQuery(id+"F0.wireOp",EDGE,"E5"),sQuery(id+"F0.wireOp",EDGE,"E6"),sQuery(id+"F0.wireOp",EDGE,"E7"),sQuery(id+"F0.wireOp",EDGE,"E8"),sQuery(id+"F0.wireOp",EDGE,"E9"),sQuery(id+"F0.wireOp",EDGE,"E10.0"),sQuery(id+"F0.wireOp",EDGE,"E10.1"),sQuery(id+"F0.wireOp",EDGE,"E10.2"),sQuery(id+"F0.wireOp",EDGE,"E10.3"),sQuery(id+"F0.wireOp",EDGE,"E10.4"),sQuery(id+"F0.wireOp",EDGE,"E10.5"),sQuery(id+"F0.wireOp",EDGE,"E11"),sQuery(id+"F0.wireOp",EDGE,"E12"),sQuery(id+"F0.wireOp",EDGE,"E13"),sQuery(id+"F0.wireOp",EDGE,"E14"),sQuery(id+"F0.wireOp",EDGE,"E15"),sQuery(id+"F0.wireOp",EDGE,"E16"),sQuery(id+"F0.wireOp",EDGE,"E17"),sQuery(id+"F0.wireOp",EDGE,"E18"),sQuery(id+"F0.wireOp",EDGE,"E19")])],"isStart":false})})});}
            var sketch = newSketch(context, id + "F17", { "sketchPlane" : qUnion([Q0])});
            skLineSegment(sketch, "E70", {"start": v(7.57, 0) * mm, "end": v(13, 3.13) * mm});
            skLineSegment(sketch, "E71", {"start": v(13, 3.13) * mm, "end": v(13, -3.13) * mm});
            skLineSegment(sketch, "E72", {"start": v(13, -3.13) * mm, "end": v(7.57, 0) * mm});
            skSolve(sketch);
        }
        {
            var Q0;
            Q0 = qSketchRegion(id + "F17", true);
            extrude(context, id + "F18", {"entities" : qUnion([Q0]), "operationType" : NewBodyOperationType.REMOVE, "oppositeDirection" : true, "depth" : 25 * mm});
        }
        {
            var Q0;
            {var subQ0=sQuery(id+"F3.wireOp",EDGE,"E39.5");Q0=makeQuery(id+"F4.boolean.opBoolean","SPLIT",FACE,{"disambiguationData":[TD([makeQuery(id+"F4.opExtrude","SWEPT_FACE",FACE,{"disambiguationData":[OSD([subQ0])]})])],"derivedFrom":makeQuery(id+"F2.opChamfer","SPLIT",FACE,{"disambiguationData":[OD(6.0)],"derivedFrom":makeQuery(id+"F1.opExtrude","CAP_FACE",FACE,{"disambiguationData":[OSD([sQuery(id+"F0.wireOp",EDGE,"E0.0"),sQuery(id+"F0.wireOp",EDGE,"E0.1"),sQuery(id+"F0.wireOp",EDGE,"E0.2"),sQuery(id+"F0.wireOp",EDGE,"E0.3"),sQuery(id+"F0.wireOp",EDGE,"E0.4"),sQuery(id+"F0.wireOp",EDGE,"E0.5"),sQuery(id+"F0.wireOp",EDGE,"E1"),sQuery(id+"F0.wireOp",EDGE,"E2"),sQuery(id+"F0.wireOp",EDGE,"E3"),sQuery(id+"F0.wireOp",EDGE,"E4"),sQuery(id+"F0.wireOp",EDGE,"E5"),sQuery(id+"F0.wireOp",EDGE,"E6"),sQuery(id+"F0.wireOp",EDGE,"E7"),sQuery(id+"F0.wireOp",EDGE,"E8"),sQuery(id+"F0.wireOp",EDGE,"E9"),sQuery(id+"F0.wireOp",EDGE,"E10.0"),sQuery(id+"F0.wireOp",EDGE,"E10.1"),sQuery(id+"F0.wireOp",EDGE,"E10.2"),sQuery(id+"F0.wireOp",EDGE,"E10.3"),sQuery(id+"F0.wireOp",EDGE,"E10.4"),sQuery(id+"F0.wireOp",EDGE,"E10.5"),sQuery(id+"F0.wireOp",EDGE,"E11"),sQuery(id+"F0.wireOp",EDGE,"E12"),sQuery(id+"F0.wireOp",EDGE,"E13"),sQuery(id+"F0.wireOp",EDGE,"E14"),sQuery(id+"F0.wireOp",EDGE,"E15"),sQuery(id+"F0.wireOp",EDGE,"E16"),sQuery(id+"F0.wireOp",EDGE,"E17"),sQuery(id+"F0.wireOp",EDGE,"E18"),sQuery(id+"F0.wireOp",EDGE,"E19")])],"isStart":false})})});}
            var sketch = newSketch(context, id + "F19", { "sketchPlane" : qUnion([Q0])});
            skLineSegment(sketch, "E73", {"start": v(-9.21, -9.7) * mm, "end": v(-3.79, -6.56) * mm});
            skPoint(sketch, "E73.startSnap0", {"position": v(-2.79, -9.7) * mm});
            skLineSegment(sketch, "E74", {"start": v(-3.79, -6.56) * mm, "end": v(-3.79, -12.83) * mm});
            skLineSegment(sketch, "E75", {"start": v(-3.79, -12.83) * mm, "end": v(-9.21, -9.7) * mm});
            skSolve(sketch);
        }
        {
            var Q0;
            Q0 = qSketchRegion(id + "F19", true);
            extrude(context, id + "F20", {"entities" : qUnion([Q0]), "operationType" : NewBodyOperationType.REMOVE, "oppositeDirection" : true, "depth" : 25 * mm});
        }
        {
            var Q0;
            {var subQ3=sQuery(id+"F3.wireOp",EDGE,"E39.4");Q0=makeQuery(id+"F4.boolean.opBoolean","SPLIT",FACE,{"disambiguationData":[TD([makeQuery(id+"F4.opExtrude","SWEPT_FACE",FACE,{"disambiguationData":[OSD([subQ3])]})])],"derivedFrom":makeQuery(id+"F2.opChamfer","SPLIT",FACE,{"disambiguationData":[OD(6.0)],"derivedFrom":makeQuery(id+"F1.opExtrude","CAP_FACE",FACE,{"disambiguationData":[OSD([sQuery(id+"F0.wireOp",EDGE,"E0.0"),sQuery(id+"F0.wireOp",EDGE,"E0.1"),sQuery(id+"F0.wireOp",EDGE,"E0.2"),sQuery(id+"F0.wireOp",EDGE,"E0.3"),sQuery(id+"F0.wireOp",EDGE,"E0.4"),sQuery(id+"F0.wireOp",EDGE,"E0.5"),sQuery(id+"F0.wireOp",EDGE,"E1"),sQuery(id+"F0.wireOp",EDGE,"E2"),sQuery(id+"F0.wireOp",EDGE,"E3"),sQuery(id+"F0.wireOp",EDGE,"E4"),sQuery(id+"F0.wireOp",EDGE,"E5"),sQuery(id+"F0.wireOp",EDGE,"E6"),sQuery(id+"F0.wireOp",EDGE,"E7"),sQuery(id+"F0.wireOp",EDGE,"E8"),sQuery(id+"F0.wireOp",EDGE,"E9"),sQuery(id+"F0.wireOp",EDGE,"E10.0"),sQuery(id+"F0.wireOp",EDGE,"E10.1"),sQuery(id+"F0.wireOp",EDGE,"E10.2"),sQuery(id+"F0.wireOp",EDGE,"E10.3"),sQuery(id+"F0.wireOp",EDGE,"E10.4"),sQuery(id+"F0.wireOp",EDGE,"E10.5"),sQuery(id+"F0.wireOp",EDGE,"E11"),sQuery(id+"F0.wireOp",EDGE,"E12"),sQuery(id+"F0.wireOp",EDGE,"E13"),sQuery(id+"F0.wireOp",EDGE,"E14"),sQuery(id+"F0.wireOp",EDGE,"E15"),sQuery(id+"F0.wireOp",EDGE,"E16"),sQuery(id+"F0.wireOp",EDGE,"E17"),sQuery(id+"F0.wireOp",EDGE,"E18"),sQuery(id+"F0.wireOp",EDGE,"E19")])],"isStart":false})})});}
            var sketch = newSketch(context, id + "F21", { "sketchPlane" : qUnion([Q0])});
            skLineSegment(sketch, "E76", {"start": v(9.21, -9.7) * mm, "end": v(3.79, -6.56) * mm});
            skLineSegment(sketch, "E77", {"start": v(3.79, -6.56) * mm, "end": v(3.79, -12.83) * mm});
            skLineSegment(sketch, "E78", {"start": v(3.79, -12.83) * mm, "end": v(9.21, -9.7) * mm});
            skSolve(sketch);
        }
        {
            var Q0;
            Q0 = qSketchRegion(id + "F21", true);
            extrude(context, id + "F22", {"entities" : qUnion([Q0]), "operationType" : NewBodyOperationType.REMOVE, "oppositeDirection" : true, "depth" : 25 * mm});
        }
        {
            var Q0;
            Q0=makeQuery(id+"F12.boolean.opBoolean","COPY",EDGE,{"derivedFrom":makeQuery(id+"F12.opExtrude","CAP_EDGE",EDGE,{"disambiguationData":[OSD([sQuery(id+"F11.wireOp",EDGE,"E61")])],"isStart":true})});
            var Q1;
            Q1=makeQuery(id+"F12.boolean.opBoolean","COPY",EDGE,{"derivedFrom":makeQuery(id+"F12.opExtrude","CAP_EDGE",EDGE,{"disambiguationData":[OSD([sQuery(id+"F11.wireOp",EDGE,"E62")])],"isStart":true})});
            var Q2;
            Q2=makeQuery(id+"F12.boolean.opBoolean","COPY",EDGE,{"derivedFrom":makeQuery(id+"F12.opExtrude","CAP_EDGE",EDGE,{"disambiguationData":[OSD([sQuery(id+"F11.wireOp",EDGE,"E63")])],"isStart":true})});
            var Q3;
            Q3=makeQuery(id+"F14.boolean.opBoolean","COPY",EDGE,{"derivedFrom":makeQuery(id+"F14.opExtrude","CAP_EDGE",EDGE,{"disambiguationData":[OSD([sQuery(id+"F13.wireOp",EDGE,"E65")])],"isStart":true})});
            var Q4;
            Q4=makeQuery(id+"F14.boolean.opBoolean","COPY",EDGE,{"derivedFrom":makeQuery(id+"F14.opExtrude","CAP_EDGE",EDGE,{"disambiguationData":[OSD([sQuery(id+"F13.wireOp",EDGE,"E64")])],"isStart":true})});
            var Q5;
            Q5=makeQuery(id+"F14.boolean.opBoolean","COPY",EDGE,{"derivedFrom":makeQuery(id+"F14.opExtrude","CAP_EDGE",EDGE,{"disambiguationData":[OSD([sQuery(id+"F13.wireOp",EDGE,"E66")])],"isStart":true})});
            var Q6;
            Q6=makeQuery(id+"F18.boolean.opBoolean","COPY",EDGE,{"derivedFrom":makeQuery(id+"F18.opExtrude","CAP_EDGE",EDGE,{"disambiguationData":[OSD([sQuery(id+"F17.wireOp",EDGE,"E70")])],"isStart":true})});
            var Q7;
            Q7=makeQuery(id+"F18.boolean.opBoolean","COPY",EDGE,{"derivedFrom":makeQuery(id+"F18.opExtrude","CAP_EDGE",EDGE,{"disambiguationData":[OSD([sQuery(id+"F17.wireOp",EDGE,"E72")])],"isStart":true})});
            var Q8;
            Q8=makeQuery(id+"F18.boolean.opBoolean","COPY",EDGE,{"derivedFrom":makeQuery(id+"F18.opExtrude","CAP_EDGE",EDGE,{"disambiguationData":[OSD([sQuery(id+"F17.wireOp",EDGE,"E71")])],"isStart":true})});
            var Q9;
            Q9=makeQuery(id+"F22.boolean.opBoolean","COPY",EDGE,{"derivedFrom":makeQuery(id+"F22.opExtrude","CAP_EDGE",EDGE,{"disambiguationData":[OSD([sQuery(id+"F21.wireOp",EDGE,"E76")])],"isStart":true})});
            var Q10;
            Q10=makeQuery(id+"F22.boolean.opBoolean","COPY",EDGE,{"derivedFrom":makeQuery(id+"F22.opExtrude","CAP_EDGE",EDGE,{"disambiguationData":[OSD([sQuery(id+"F21.wireOp",EDGE,"E77")])],"isStart":true})});
            var Q11;
            Q11=makeQuery(id+"F22.boolean.opBoolean","COPY",EDGE,{"derivedFrom":makeQuery(id+"F22.opExtrude","CAP_EDGE",EDGE,{"disambiguationData":[OSD([sQuery(id+"F21.wireOp",EDGE,"E78")])],"isStart":true})});
            var Q12;
            Q12=makeQuery(id+"F20.boolean.opBoolean","COPY",EDGE,{"derivedFrom":makeQuery(id+"F20.opExtrude","CAP_EDGE",EDGE,{"disambiguationData":[OSD([sQuery(id+"F19.wireOp",EDGE,"E73")])],"isStart":true})});
            var Q13;
            Q13=makeQuery(id+"F20.boolean.opBoolean","COPY",EDGE,{"derivedFrom":makeQuery(id+"F20.opExtrude","CAP_EDGE",EDGE,{"disambiguationData":[OSD([sQuery(id+"F19.wireOp",EDGE,"E74")])],"isStart":true})});
            var Q14;
            Q14=makeQuery(id+"F20.boolean.opBoolean","COPY",EDGE,{"derivedFrom":makeQuery(id+"F20.opExtrude","CAP_EDGE",EDGE,{"disambiguationData":[OSD([sQuery(id+"F19.wireOp",EDGE,"E75")])],"isStart":true})});
            var Q15;
            Q15=makeQuery(id+"F16.boolean.opBoolean","COPY",EDGE,{"derivedFrom":makeQuery(id+"F16.opExtrude","CAP_EDGE",EDGE,{"disambiguationData":[OSD([sQuery(id+"F15.wireOp",EDGE,"E68")])],"isStart":true})});
            var Q16;
            Q16=makeQuery(id+"F16.boolean.opBoolean","COPY",EDGE,{"derivedFrom":makeQuery(id+"F16.opExtrude","CAP_EDGE",EDGE,{"disambiguationData":[OSD([sQuery(id+"F15.wireOp",EDGE,"E67")])],"isStart":true})});
            var Q17;
            Q17=makeQuery(id+"F16.boolean.opBoolean","COPY",EDGE,{"derivedFrom":makeQuery(id+"F16.opExtrude","CAP_EDGE",EDGE,{"disambiguationData":[OSD([sQuery(id+"F15.wireOp",EDGE,"E69")])],"isStart":true})});
            var Q18;
            {var subQ0=sQuery(id+"F5.wireOp",EDGE,"E59.1");Q18=makeQuery(id+"F14.boolean.opBoolean","INTERSECT",EDGE,{"derivedFrom":[makeQuery(id+"F6.boolean.opBoolean","SPLIT",FACE,{"disambiguationData":[TD([makeQuery(id+"F6.opExtrude","SWEPT_FACE",FACE,{"disambiguationData":[OSD([subQ0])]})])],"derivedFrom":makeQuery(id+"F2.opChamfer","SPLIT",FACE,{"disambiguationData":[OD(6.0)],"derivedFrom":makeQuery(id+"F1.opExtrude","CAP_FACE",FACE,{"disambiguationData":[OSD([sQuery(id+"F0.wireOp",EDGE,"E0.0"),sQuery(id+"F0.wireOp",EDGE,"E0.1"),sQuery(id+"F0.wireOp",EDGE,"E0.2"),sQuery(id+"F0.wireOp",EDGE,"E0.3"),sQuery(id+"F0.wireOp",EDGE,"E0.4"),sQuery(id+"F0.wireOp",EDGE,"E0.5"),sQuery(id+"F0.wireOp",EDGE,"E1"),sQuery(id+"F0.wireOp",EDGE,"E2"),sQuery(id+"F0.wireOp",EDGE,"E3"),sQuery(id+"F0.wireOp",EDGE,"E4"),sQuery(id+"F0.wireOp",EDGE,"E5"),sQuery(id+"F0.wireOp",EDGE,"E6"),sQuery(id+"F0.wireOp",EDGE,"E7"),sQuery(id+"F0.wireOp",EDGE,"E8"),sQuery(id+"F0.wireOp",EDGE,"E9"),sQuery(id+"F0.wireOp",EDGE,"E10.0"),sQuery(id+"F0.wireOp",EDGE,"E10.1"),sQuery(id+"F0.wireOp",EDGE,"E10.2"),sQuery(id+"F0.wireOp",EDGE,"E10.3"),sQuery(id+"F0.wireOp",EDGE,"E10.4"),sQuery(id+"F0.wireOp",EDGE,"E10.5"),sQuery(id+"F0.wireOp",EDGE,"E11"),sQuery(id+"F0.wireOp",EDGE,"E12"),sQuery(id+"F0.wireOp",EDGE,"E13"),sQuery(id+"F0.wireOp",EDGE,"E14"),sQuery(id+"F0.wireOp",EDGE,"E15"),sQuery(id+"F0.wireOp",EDGE,"E16"),sQuery(id+"F0.wireOp",EDGE,"E17"),sQuery(id+"F0.wireOp",EDGE,"E18"),sQuery(id+"F0.wireOp",EDGE,"E19")])],"isStart":true})})}),makeQuery(id+"F14.opExtrude","SWEPT_FACE",FACE,{"disambiguationData":[OSD([sQuery(id+"F13.wireOp",EDGE,"E64")])]})]});}
            var Q19;
            {var subQ0=sQuery(id+"F5.wireOp",EDGE,"E59.1");Q19=makeQuery(id+"F14.boolean.opBoolean","INTERSECT",EDGE,{"derivedFrom":[makeQuery(id+"F6.boolean.opBoolean","SPLIT",FACE,{"disambiguationData":[TD([makeQuery(id+"F6.opExtrude","SWEPT_FACE",FACE,{"disambiguationData":[OSD([subQ0])]})])],"derivedFrom":makeQuery(id+"F2.opChamfer","SPLIT",FACE,{"disambiguationData":[OD(6.0)],"derivedFrom":makeQuery(id+"F1.opExtrude","CAP_FACE",FACE,{"disambiguationData":[OSD([sQuery(id+"F0.wireOp",EDGE,"E0.0"),sQuery(id+"F0.wireOp",EDGE,"E0.1"),sQuery(id+"F0.wireOp",EDGE,"E0.2"),sQuery(id+"F0.wireOp",EDGE,"E0.3"),sQuery(id+"F0.wireOp",EDGE,"E0.4"),sQuery(id+"F0.wireOp",EDGE,"E0.5"),sQuery(id+"F0.wireOp",EDGE,"E1"),sQuery(id+"F0.wireOp",EDGE,"E2"),sQuery(id+"F0.wireOp",EDGE,"E3"),sQuery(id+"F0.wireOp",EDGE,"E4"),sQuery(id+"F0.wireOp",EDGE,"E5"),sQuery(id+"F0.wireOp",EDGE,"E6"),sQuery(id+"F0.wireOp",EDGE,"E7"),sQuery(id+"F0.wireOp",EDGE,"E8"),sQuery(id+"F0.wireOp",EDGE,"E9"),sQuery(id+"F0.wireOp",EDGE,"E10.0"),sQuery(id+"F0.wireOp",EDGE,"E10.1"),sQuery(id+"F0.wireOp",EDGE,"E10.2"),sQuery(id+"F0.wireOp",EDGE,"E10.3"),sQuery(id+"F0.wireOp",EDGE,"E10.4"),sQuery(id+"F0.wireOp",EDGE,"E10.5"),sQuery(id+"F0.wireOp",EDGE,"E11"),sQuery(id+"F0.wireOp",EDGE,"E12"),sQuery(id+"F0.wireOp",EDGE,"E13"),sQuery(id+"F0.wireOp",EDGE,"E14"),sQuery(id+"F0.wireOp",EDGE,"E15"),sQuery(id+"F0.wireOp",EDGE,"E16"),sQuery(id+"F0.wireOp",EDGE,"E17"),sQuery(id+"F0.wireOp",EDGE,"E18"),sQuery(id+"F0.wireOp",EDGE,"E19")])],"isStart":true})})}),makeQuery(id+"F14.opExtrude","SWEPT_FACE",FACE,{"disambiguationData":[OSD([sQuery(id+"F13.wireOp",EDGE,"E65")])]})]});}
            var Q20;
            {var subQ0=sQuery(id+"F5.wireOp",EDGE,"E59.1");Q20=makeQuery(id+"F14.boolean.opBoolean","INTERSECT",EDGE,{"derivedFrom":[makeQuery(id+"F6.boolean.opBoolean","SPLIT",FACE,{"disambiguationData":[TD([makeQuery(id+"F6.opExtrude","SWEPT_FACE",FACE,{"disambiguationData":[OSD([subQ0])]})])],"derivedFrom":makeQuery(id+"F2.opChamfer","SPLIT",FACE,{"disambiguationData":[OD(6.0)],"derivedFrom":makeQuery(id+"F1.opExtrude","CAP_FACE",FACE,{"disambiguationData":[OSD([sQuery(id+"F0.wireOp",EDGE,"E0.0"),sQuery(id+"F0.wireOp",EDGE,"E0.1"),sQuery(id+"F0.wireOp",EDGE,"E0.2"),sQuery(id+"F0.wireOp",EDGE,"E0.3"),sQuery(id+"F0.wireOp",EDGE,"E0.4"),sQuery(id+"F0.wireOp",EDGE,"E0.5"),sQuery(id+"F0.wireOp",EDGE,"E1"),sQuery(id+"F0.wireOp",EDGE,"E2"),sQuery(id+"F0.wireOp",EDGE,"E3"),sQuery(id+"F0.wireOp",EDGE,"E4"),sQuery(id+"F0.wireOp",EDGE,"E5"),sQuery(id+"F0.wireOp",EDGE,"E6"),sQuery(id+"F0.wireOp",EDGE,"E7"),sQuery(id+"F0.wireOp",EDGE,"E8"),sQuery(id+"F0.wireOp",EDGE,"E9"),sQuery(id+"F0.wireOp",EDGE,"E10.0"),sQuery(id+"F0.wireOp",EDGE,"E10.1"),sQuery(id+"F0.wireOp",EDGE,"E10.2"),sQuery(id+"F0.wireOp",EDGE,"E10.3"),sQuery(id+"F0.wireOp",EDGE,"E10.4"),sQuery(id+"F0.wireOp",EDGE,"E10.5"),sQuery(id+"F0.wireOp",EDGE,"E11"),sQuery(id+"F0.wireOp",EDGE,"E12"),sQuery(id+"F0.wireOp",EDGE,"E13"),sQuery(id+"F0.wireOp",EDGE,"E14"),sQuery(id+"F0.wireOp",EDGE,"E15"),sQuery(id+"F0.wireOp",EDGE,"E16"),sQuery(id+"F0.wireOp",EDGE,"E17"),sQuery(id+"F0.wireOp",EDGE,"E18"),sQuery(id+"F0.wireOp",EDGE,"E19")])],"isStart":true})})}),makeQuery(id+"F14.opExtrude","SWEPT_FACE",FACE,{"disambiguationData":[OSD([sQuery(id+"F13.wireOp",EDGE,"E66")])]})]});}
            var Q21;
            {var subQ3=sQuery(id+"F5.wireOp",EDGE,"E59.2");Q21=makeQuery(id+"F12.boolean.opBoolean","INTERSECT",EDGE,{"derivedFrom":[makeQuery(id+"F6.boolean.opBoolean","SPLIT",FACE,{"disambiguationData":[TD([makeQuery(id+"F6.opExtrude","SWEPT_FACE",FACE,{"disambiguationData":[OSD([subQ3])]})])],"derivedFrom":makeQuery(id+"F2.opChamfer","SPLIT",FACE,{"disambiguationData":[OD(6.0)],"derivedFrom":makeQuery(id+"F1.opExtrude","CAP_FACE",FACE,{"disambiguationData":[OSD([sQuery(id+"F0.wireOp",EDGE,"E0.0"),sQuery(id+"F0.wireOp",EDGE,"E0.1"),sQuery(id+"F0.wireOp",EDGE,"E0.2"),sQuery(id+"F0.wireOp",EDGE,"E0.3"),sQuery(id+"F0.wireOp",EDGE,"E0.4"),sQuery(id+"F0.wireOp",EDGE,"E0.5"),sQuery(id+"F0.wireOp",EDGE,"E1"),sQuery(id+"F0.wireOp",EDGE,"E2"),sQuery(id+"F0.wireOp",EDGE,"E3"),sQuery(id+"F0.wireOp",EDGE,"E4"),sQuery(id+"F0.wireOp",EDGE,"E5"),sQuery(id+"F0.wireOp",EDGE,"E6"),sQuery(id+"F0.wireOp",EDGE,"E7"),sQuery(id+"F0.wireOp",EDGE,"E8"),sQuery(id+"F0.wireOp",EDGE,"E9"),sQuery(id+"F0.wireOp",EDGE,"E10.0"),sQuery(id+"F0.wireOp",EDGE,"E10.1"),sQuery(id+"F0.wireOp",EDGE,"E10.2"),sQuery(id+"F0.wireOp",EDGE,"E10.3"),sQuery(id+"F0.wireOp",EDGE,"E10.4"),sQuery(id+"F0.wireOp",EDGE,"E10.5"),sQuery(id+"F0.wireOp",EDGE,"E11"),sQuery(id+"F0.wireOp",EDGE,"E12"),sQuery(id+"F0.wireOp",EDGE,"E13"),sQuery(id+"F0.wireOp",EDGE,"E14"),sQuery(id+"F0.wireOp",EDGE,"E15"),sQuery(id+"F0.wireOp",EDGE,"E16"),sQuery(id+"F0.wireOp",EDGE,"E17"),sQuery(id+"F0.wireOp",EDGE,"E18"),sQuery(id+"F0.wireOp",EDGE,"E19")])],"isStart":true})})}),makeQuery(id+"F12.opExtrude","SWEPT_FACE",FACE,{"disambiguationData":[OSD([sQuery(id+"F11.wireOp",EDGE,"E61")])]})]});}
            var Q22;
            {var subQ3=sQuery(id+"F5.wireOp",EDGE,"E59.2");Q22=makeQuery(id+"F12.boolean.opBoolean","INTERSECT",EDGE,{"derivedFrom":[makeQuery(id+"F6.boolean.opBoolean","SPLIT",FACE,{"disambiguationData":[TD([makeQuery(id+"F6.opExtrude","SWEPT_FACE",FACE,{"disambiguationData":[OSD([subQ3])]})])],"derivedFrom":makeQuery(id+"F2.opChamfer","SPLIT",FACE,{"disambiguationData":[OD(6.0)],"derivedFrom":makeQuery(id+"F1.opExtrude","CAP_FACE",FACE,{"disambiguationData":[OSD([sQuery(id+"F0.wireOp",EDGE,"E0.0"),sQuery(id+"F0.wireOp",EDGE,"E0.1"),sQuery(id+"F0.wireOp",EDGE,"E0.2"),sQuery(id+"F0.wireOp",EDGE,"E0.3"),sQuery(id+"F0.wireOp",EDGE,"E0.4"),sQuery(id+"F0.wireOp",EDGE,"E0.5"),sQuery(id+"F0.wireOp",EDGE,"E1"),sQuery(id+"F0.wireOp",EDGE,"E2"),sQuery(id+"F0.wireOp",EDGE,"E3"),sQuery(id+"F0.wireOp",EDGE,"E4"),sQuery(id+"F0.wireOp",EDGE,"E5"),sQuery(id+"F0.wireOp",EDGE,"E6"),sQuery(id+"F0.wireOp",EDGE,"E7"),sQuery(id+"F0.wireOp",EDGE,"E8"),sQuery(id+"F0.wireOp",EDGE,"E9"),sQuery(id+"F0.wireOp",EDGE,"E10.0"),sQuery(id+"F0.wireOp",EDGE,"E10.1"),sQuery(id+"F0.wireOp",EDGE,"E10.2"),sQuery(id+"F0.wireOp",EDGE,"E10.3"),sQuery(id+"F0.wireOp",EDGE,"E10.4"),sQuery(id+"F0.wireOp",EDGE,"E10.5"),sQuery(id+"F0.wireOp",EDGE,"E11"),sQuery(id+"F0.wireOp",EDGE,"E12"),sQuery(id+"F0.wireOp",EDGE,"E13"),sQuery(id+"F0.wireOp",EDGE,"E14"),sQuery(id+"F0.wireOp",EDGE,"E15"),sQuery(id+"F0.wireOp",EDGE,"E16"),sQuery(id+"F0.wireOp",EDGE,"E17"),sQuery(id+"F0.wireOp",EDGE,"E18"),sQuery(id+"F0.wireOp",EDGE,"E19")])],"isStart":true})})}),makeQuery(id+"F12.opExtrude","SWEPT_FACE",FACE,{"disambiguationData":[OSD([sQuery(id+"F11.wireOp",EDGE,"E62")])]})]});}
            var Q23;
            {var subQ3=sQuery(id+"F5.wireOp",EDGE,"E59.2");Q23=makeQuery(id+"F12.boolean.opBoolean","INTERSECT",EDGE,{"derivedFrom":[makeQuery(id+"F6.boolean.opBoolean","SPLIT",FACE,{"disambiguationData":[TD([makeQuery(id+"F6.opExtrude","SWEPT_FACE",FACE,{"disambiguationData":[OSD([subQ3])]})])],"derivedFrom":makeQuery(id+"F2.opChamfer","SPLIT",FACE,{"disambiguationData":[OD(6.0)],"derivedFrom":makeQuery(id+"F1.opExtrude","CAP_FACE",FACE,{"disambiguationData":[OSD([sQuery(id+"F0.wireOp",EDGE,"E0.0"),sQuery(id+"F0.wireOp",EDGE,"E0.1"),sQuery(id+"F0.wireOp",EDGE,"E0.2"),sQuery(id+"F0.wireOp",EDGE,"E0.3"),sQuery(id+"F0.wireOp",EDGE,"E0.4"),sQuery(id+"F0.wireOp",EDGE,"E0.5"),sQuery(id+"F0.wireOp",EDGE,"E1"),sQuery(id+"F0.wireOp",EDGE,"E2"),sQuery(id+"F0.wireOp",EDGE,"E3"),sQuery(id+"F0.wireOp",EDGE,"E4"),sQuery(id+"F0.wireOp",EDGE,"E5"),sQuery(id+"F0.wireOp",EDGE,"E6"),sQuery(id+"F0.wireOp",EDGE,"E7"),sQuery(id+"F0.wireOp",EDGE,"E8"),sQuery(id+"F0.wireOp",EDGE,"E9"),sQuery(id+"F0.wireOp",EDGE,"E10.0"),sQuery(id+"F0.wireOp",EDGE,"E10.1"),sQuery(id+"F0.wireOp",EDGE,"E10.2"),sQuery(id+"F0.wireOp",EDGE,"E10.3"),sQuery(id+"F0.wireOp",EDGE,"E10.4"),sQuery(id+"F0.wireOp",EDGE,"E10.5"),sQuery(id+"F0.wireOp",EDGE,"E11"),sQuery(id+"F0.wireOp",EDGE,"E12"),sQuery(id+"F0.wireOp",EDGE,"E13"),sQuery(id+"F0.wireOp",EDGE,"E14"),sQuery(id+"F0.wireOp",EDGE,"E15"),sQuery(id+"F0.wireOp",EDGE,"E16"),sQuery(id+"F0.wireOp",EDGE,"E17"),sQuery(id+"F0.wireOp",EDGE,"E18"),sQuery(id+"F0.wireOp",EDGE,"E19")])],"isStart":true})})}),makeQuery(id+"F12.opExtrude","SWEPT_FACE",FACE,{"disambiguationData":[OSD([sQuery(id+"F11.wireOp",EDGE,"E63")])]})]});}
            var Q24;
            {var subQ3=sQuery(id+"F5.wireOp",EDGE,"E59.3");Q24=makeQuery(id+"F16.boolean.opBoolean","INTERSECT",EDGE,{"derivedFrom":[makeQuery(id+"F6.boolean.opBoolean","SPLIT",FACE,{"disambiguationData":[TD([makeQuery(id+"F6.opExtrude","SWEPT_FACE",FACE,{"disambiguationData":[OSD([subQ3])]})])],"derivedFrom":makeQuery(id+"F2.opChamfer","SPLIT",FACE,{"disambiguationData":[OD(6.0)],"derivedFrom":makeQuery(id+"F1.opExtrude","CAP_FACE",FACE,{"disambiguationData":[OSD([sQuery(id+"F0.wireOp",EDGE,"E0.0"),sQuery(id+"F0.wireOp",EDGE,"E0.1"),sQuery(id+"F0.wireOp",EDGE,"E0.2"),sQuery(id+"F0.wireOp",EDGE,"E0.3"),sQuery(id+"F0.wireOp",EDGE,"E0.4"),sQuery(id+"F0.wireOp",EDGE,"E0.5"),sQuery(id+"F0.wireOp",EDGE,"E1"),sQuery(id+"F0.wireOp",EDGE,"E2"),sQuery(id+"F0.wireOp",EDGE,"E3"),sQuery(id+"F0.wireOp",EDGE,"E4"),sQuery(id+"F0.wireOp",EDGE,"E5"),sQuery(id+"F0.wireOp",EDGE,"E6"),sQuery(id+"F0.wireOp",EDGE,"E7"),sQuery(id+"F0.wireOp",EDGE,"E8"),sQuery(id+"F0.wireOp",EDGE,"E9"),sQuery(id+"F0.wireOp",EDGE,"E10.0"),sQuery(id+"F0.wireOp",EDGE,"E10.1"),sQuery(id+"F0.wireOp",EDGE,"E10.2"),sQuery(id+"F0.wireOp",EDGE,"E10.3"),sQuery(id+"F0.wireOp",EDGE,"E10.4"),sQuery(id+"F0.wireOp",EDGE,"E10.5"),sQuery(id+"F0.wireOp",EDGE,"E11"),sQuery(id+"F0.wireOp",EDGE,"E12"),sQuery(id+"F0.wireOp",EDGE,"E13"),sQuery(id+"F0.wireOp",EDGE,"E14"),sQuery(id+"F0.wireOp",EDGE,"E15"),sQuery(id+"F0.wireOp",EDGE,"E16"),sQuery(id+"F0.wireOp",EDGE,"E17"),sQuery(id+"F0.wireOp",EDGE,"E18"),sQuery(id+"F0.wireOp",EDGE,"E19")])],"isStart":true})})}),makeQuery(id+"F16.opExtrude","SWEPT_FACE",FACE,{"disambiguationData":[OSD([sQuery(id+"F15.wireOp",EDGE,"E67")])]})]});}
            var Q25;
            {var subQ3=sQuery(id+"F5.wireOp",EDGE,"E59.3");Q25=makeQuery(id+"F16.boolean.opBoolean","INTERSECT",EDGE,{"derivedFrom":[makeQuery(id+"F6.boolean.opBoolean","SPLIT",FACE,{"disambiguationData":[TD([makeQuery(id+"F6.opExtrude","SWEPT_FACE",FACE,{"disambiguationData":[OSD([subQ3])]})])],"derivedFrom":makeQuery(id+"F2.opChamfer","SPLIT",FACE,{"disambiguationData":[OD(6.0)],"derivedFrom":makeQuery(id+"F1.opExtrude","CAP_FACE",FACE,{"disambiguationData":[OSD([sQuery(id+"F0.wireOp",EDGE,"E0.0"),sQuery(id+"F0.wireOp",EDGE,"E0.1"),sQuery(id+"F0.wireOp",EDGE,"E0.2"),sQuery(id+"F0.wireOp",EDGE,"E0.3"),sQuery(id+"F0.wireOp",EDGE,"E0.4"),sQuery(id+"F0.wireOp",EDGE,"E0.5"),sQuery(id+"F0.wireOp",EDGE,"E1"),sQuery(id+"F0.wireOp",EDGE,"E2"),sQuery(id+"F0.wireOp",EDGE,"E3"),sQuery(id+"F0.wireOp",EDGE,"E4"),sQuery(id+"F0.wireOp",EDGE,"E5"),sQuery(id+"F0.wireOp",EDGE,"E6"),sQuery(id+"F0.wireOp",EDGE,"E7"),sQuery(id+"F0.wireOp",EDGE,"E8"),sQuery(id+"F0.wireOp",EDGE,"E9"),sQuery(id+"F0.wireOp",EDGE,"E10.0"),sQuery(id+"F0.wireOp",EDGE,"E10.1"),sQuery(id+"F0.wireOp",EDGE,"E10.2"),sQuery(id+"F0.wireOp",EDGE,"E10.3"),sQuery(id+"F0.wireOp",EDGE,"E10.4"),sQuery(id+"F0.wireOp",EDGE,"E10.5"),sQuery(id+"F0.wireOp",EDGE,"E11"),sQuery(id+"F0.wireOp",EDGE,"E12"),sQuery(id+"F0.wireOp",EDGE,"E13"),sQuery(id+"F0.wireOp",EDGE,"E14"),sQuery(id+"F0.wireOp",EDGE,"E15"),sQuery(id+"F0.wireOp",EDGE,"E16"),sQuery(id+"F0.wireOp",EDGE,"E17"),sQuery(id+"F0.wireOp",EDGE,"E18"),sQuery(id+"F0.wireOp",EDGE,"E19")])],"isStart":true})})}),makeQuery(id+"F16.opExtrude","SWEPT_FACE",FACE,{"disambiguationData":[OSD([sQuery(id+"F15.wireOp",EDGE,"E68")])]})]});}
            var Q26;
            {var subQ3=sQuery(id+"F5.wireOp",EDGE,"E59.3");Q26=makeQuery(id+"F16.boolean.opBoolean","INTERSECT",EDGE,{"derivedFrom":[makeQuery(id+"F6.boolean.opBoolean","SPLIT",FACE,{"disambiguationData":[TD([makeQuery(id+"F6.opExtrude","SWEPT_FACE",FACE,{"disambiguationData":[OSD([subQ3])]})])],"derivedFrom":makeQuery(id+"F2.opChamfer","SPLIT",FACE,{"disambiguationData":[OD(6.0)],"derivedFrom":makeQuery(id+"F1.opExtrude","CAP_FACE",FACE,{"disambiguationData":[OSD([sQuery(id+"F0.wireOp",EDGE,"E0.0"),sQuery(id+"F0.wireOp",EDGE,"E0.1"),sQuery(id+"F0.wireOp",EDGE,"E0.2"),sQuery(id+"F0.wireOp",EDGE,"E0.3"),sQuery(id+"F0.wireOp",EDGE,"E0.4"),sQuery(id+"F0.wireOp",EDGE,"E0.5"),sQuery(id+"F0.wireOp",EDGE,"E1"),sQuery(id+"F0.wireOp",EDGE,"E2"),sQuery(id+"F0.wireOp",EDGE,"E3"),sQuery(id+"F0.wireOp",EDGE,"E4"),sQuery(id+"F0.wireOp",EDGE,"E5"),sQuery(id+"F0.wireOp",EDGE,"E6"),sQuery(id+"F0.wireOp",EDGE,"E7"),sQuery(id+"F0.wireOp",EDGE,"E8"),sQuery(id+"F0.wireOp",EDGE,"E9"),sQuery(id+"F0.wireOp",EDGE,"E10.0"),sQuery(id+"F0.wireOp",EDGE,"E10.1"),sQuery(id+"F0.wireOp",EDGE,"E10.2"),sQuery(id+"F0.wireOp",EDGE,"E10.3"),sQuery(id+"F0.wireOp",EDGE,"E10.4"),sQuery(id+"F0.wireOp",EDGE,"E10.5"),sQuery(id+"F0.wireOp",EDGE,"E11"),sQuery(id+"F0.wireOp",EDGE,"E12"),sQuery(id+"F0.wireOp",EDGE,"E13"),sQuery(id+"F0.wireOp",EDGE,"E14"),sQuery(id+"F0.wireOp",EDGE,"E15"),sQuery(id+"F0.wireOp",EDGE,"E16"),sQuery(id+"F0.wireOp",EDGE,"E17"),sQuery(id+"F0.wireOp",EDGE,"E18"),sQuery(id+"F0.wireOp",EDGE,"E19")])],"isStart":true})})}),makeQuery(id+"F16.opExtrude","SWEPT_FACE",FACE,{"disambiguationData":[OSD([sQuery(id+"F15.wireOp",EDGE,"E69")])]})]});}
            var Q27;
            {var subQ3=sQuery(id+"F5.wireOp",EDGE,"E59.4");Q27=makeQuery(id+"F20.boolean.opBoolean","INTERSECT",EDGE,{"derivedFrom":[makeQuery(id+"F6.boolean.opBoolean","SPLIT",FACE,{"disambiguationData":[TD([makeQuery(id+"F6.opExtrude","SWEPT_FACE",FACE,{"disambiguationData":[OSD([subQ3])]})])],"derivedFrom":makeQuery(id+"F2.opChamfer","SPLIT",FACE,{"disambiguationData":[OD(6.0)],"derivedFrom":makeQuery(id+"F1.opExtrude","CAP_FACE",FACE,{"disambiguationData":[OSD([sQuery(id+"F0.wireOp",EDGE,"E0.0"),sQuery(id+"F0.wireOp",EDGE,"E0.1"),sQuery(id+"F0.wireOp",EDGE,"E0.2"),sQuery(id+"F0.wireOp",EDGE,"E0.3"),sQuery(id+"F0.wireOp",EDGE,"E0.4"),sQuery(id+"F0.wireOp",EDGE,"E0.5"),sQuery(id+"F0.wireOp",EDGE,"E1"),sQuery(id+"F0.wireOp",EDGE,"E2"),sQuery(id+"F0.wireOp",EDGE,"E3"),sQuery(id+"F0.wireOp",EDGE,"E4"),sQuery(id+"F0.wireOp",EDGE,"E5"),sQuery(id+"F0.wireOp",EDGE,"E6"),sQuery(id+"F0.wireOp",EDGE,"E7"),sQuery(id+"F0.wireOp",EDGE,"E8"),sQuery(id+"F0.wireOp",EDGE,"E9"),sQuery(id+"F0.wireOp",EDGE,"E10.0"),sQuery(id+"F0.wireOp",EDGE,"E10.1"),sQuery(id+"F0.wireOp",EDGE,"E10.2"),sQuery(id+"F0.wireOp",EDGE,"E10.3"),sQuery(id+"F0.wireOp",EDGE,"E10.4"),sQuery(id+"F0.wireOp",EDGE,"E10.5"),sQuery(id+"F0.wireOp",EDGE,"E11"),sQuery(id+"F0.wireOp",EDGE,"E12"),sQuery(id+"F0.wireOp",EDGE,"E13"),sQuery(id+"F0.wireOp",EDGE,"E14"),sQuery(id+"F0.wireOp",EDGE,"E15"),sQuery(id+"F0.wireOp",EDGE,"E16"),sQuery(id+"F0.wireOp",EDGE,"E17"),sQuery(id+"F0.wireOp",EDGE,"E18"),sQuery(id+"F0.wireOp",EDGE,"E19")])],"isStart":true})})}),makeQuery(id+"F20.opExtrude","SWEPT_FACE",FACE,{"disambiguationData":[OSD([sQuery(id+"F19.wireOp",EDGE,"E73")])]})]});}
            var Q28;
            {var subQ3=sQuery(id+"F5.wireOp",EDGE,"E59.4");Q28=makeQuery(id+"F20.boolean.opBoolean","INTERSECT",EDGE,{"derivedFrom":[makeQuery(id+"F6.boolean.opBoolean","SPLIT",FACE,{"disambiguationData":[TD([makeQuery(id+"F6.opExtrude","SWEPT_FACE",FACE,{"disambiguationData":[OSD([subQ3])]})])],"derivedFrom":makeQuery(id+"F2.opChamfer","SPLIT",FACE,{"disambiguationData":[OD(6.0)],"derivedFrom":makeQuery(id+"F1.opExtrude","CAP_FACE",FACE,{"disambiguationData":[OSD([sQuery(id+"F0.wireOp",EDGE,"E0.0"),sQuery(id+"F0.wireOp",EDGE,"E0.1"),sQuery(id+"F0.wireOp",EDGE,"E0.2"),sQuery(id+"F0.wireOp",EDGE,"E0.3"),sQuery(id+"F0.wireOp",EDGE,"E0.4"),sQuery(id+"F0.wireOp",EDGE,"E0.5"),sQuery(id+"F0.wireOp",EDGE,"E1"),sQuery(id+"F0.wireOp",EDGE,"E2"),sQuery(id+"F0.wireOp",EDGE,"E3"),sQuery(id+"F0.wireOp",EDGE,"E4"),sQuery(id+"F0.wireOp",EDGE,"E5"),sQuery(id+"F0.wireOp",EDGE,"E6"),sQuery(id+"F0.wireOp",EDGE,"E7"),sQuery(id+"F0.wireOp",EDGE,"E8"),sQuery(id+"F0.wireOp",EDGE,"E9"),sQuery(id+"F0.wireOp",EDGE,"E10.0"),sQuery(id+"F0.wireOp",EDGE,"E10.1"),sQuery(id+"F0.wireOp",EDGE,"E10.2"),sQuery(id+"F0.wireOp",EDGE,"E10.3"),sQuery(id+"F0.wireOp",EDGE,"E10.4"),sQuery(id+"F0.wireOp",EDGE,"E10.5"),sQuery(id+"F0.wireOp",EDGE,"E11"),sQuery(id+"F0.wireOp",EDGE,"E12"),sQuery(id+"F0.wireOp",EDGE,"E13"),sQuery(id+"F0.wireOp",EDGE,"E14"),sQuery(id+"F0.wireOp",EDGE,"E15"),sQuery(id+"F0.wireOp",EDGE,"E16"),sQuery(id+"F0.wireOp",EDGE,"E17"),sQuery(id+"F0.wireOp",EDGE,"E18"),sQuery(id+"F0.wireOp",EDGE,"E19")])],"isStart":true})})}),makeQuery(id+"F20.opExtrude","SWEPT_FACE",FACE,{"disambiguationData":[OSD([sQuery(id+"F19.wireOp",EDGE,"E74")])]})]});}
            var Q29;
            {var subQ3=sQuery(id+"F5.wireOp",EDGE,"E59.4");Q29=makeQuery(id+"F20.boolean.opBoolean","INTERSECT",EDGE,{"derivedFrom":[makeQuery(id+"F6.boolean.opBoolean","SPLIT",FACE,{"disambiguationData":[TD([makeQuery(id+"F6.opExtrude","SWEPT_FACE",FACE,{"disambiguationData":[OSD([subQ3])]})])],"derivedFrom":makeQuery(id+"F2.opChamfer","SPLIT",FACE,{"disambiguationData":[OD(6.0)],"derivedFrom":makeQuery(id+"F1.opExtrude","CAP_FACE",FACE,{"disambiguationData":[OSD([sQuery(id+"F0.wireOp",EDGE,"E0.0"),sQuery(id+"F0.wireOp",EDGE,"E0.1"),sQuery(id+"F0.wireOp",EDGE,"E0.2"),sQuery(id+"F0.wireOp",EDGE,"E0.3"),sQuery(id+"F0.wireOp",EDGE,"E0.4"),sQuery(id+"F0.wireOp",EDGE,"E0.5"),sQuery(id+"F0.wireOp",EDGE,"E1"),sQuery(id+"F0.wireOp",EDGE,"E2"),sQuery(id+"F0.wireOp",EDGE,"E3"),sQuery(id+"F0.wireOp",EDGE,"E4"),sQuery(id+"F0.wireOp",EDGE,"E5"),sQuery(id+"F0.wireOp",EDGE,"E6"),sQuery(id+"F0.wireOp",EDGE,"E7"),sQuery(id+"F0.wireOp",EDGE,"E8"),sQuery(id+"F0.wireOp",EDGE,"E9"),sQuery(id+"F0.wireOp",EDGE,"E10.0"),sQuery(id+"F0.wireOp",EDGE,"E10.1"),sQuery(id+"F0.wireOp",EDGE,"E10.2"),sQuery(id+"F0.wireOp",EDGE,"E10.3"),sQuery(id+"F0.wireOp",EDGE,"E10.4"),sQuery(id+"F0.wireOp",EDGE,"E10.5"),sQuery(id+"F0.wireOp",EDGE,"E11"),sQuery(id+"F0.wireOp",EDGE,"E12"),sQuery(id+"F0.wireOp",EDGE,"E13"),sQuery(id+"F0.wireOp",EDGE,"E14"),sQuery(id+"F0.wireOp",EDGE,"E15"),sQuery(id+"F0.wireOp",EDGE,"E16"),sQuery(id+"F0.wireOp",EDGE,"E17"),sQuery(id+"F0.wireOp",EDGE,"E18"),sQuery(id+"F0.wireOp",EDGE,"E19")])],"isStart":true})})}),makeQuery(id+"F20.opExtrude","SWEPT_FACE",FACE,{"disambiguationData":[OSD([sQuery(id+"F19.wireOp",EDGE,"E75")])]})]});}
            var Q30;
            {var subQ0=sQuery(id+"F5.wireOp",EDGE,"E59.5");Q30=makeQuery(id+"F22.boolean.opBoolean","INTERSECT",EDGE,{"derivedFrom":[makeQuery(id+"F6.boolean.opBoolean","SPLIT",FACE,{"disambiguationData":[TD([makeQuery(id+"F6.opExtrude","SWEPT_FACE",FACE,{"disambiguationData":[OSD([subQ0])]})])],"derivedFrom":makeQuery(id+"F2.opChamfer","SPLIT",FACE,{"disambiguationData":[OD(6.0)],"derivedFrom":makeQuery(id+"F1.opExtrude","CAP_FACE",FACE,{"disambiguationData":[OSD([sQuery(id+"F0.wireOp",EDGE,"E0.0"),sQuery(id+"F0.wireOp",EDGE,"E0.1"),sQuery(id+"F0.wireOp",EDGE,"E0.2"),sQuery(id+"F0.wireOp",EDGE,"E0.3"),sQuery(id+"F0.wireOp",EDGE,"E0.4"),sQuery(id+"F0.wireOp",EDGE,"E0.5"),sQuery(id+"F0.wireOp",EDGE,"E1"),sQuery(id+"F0.wireOp",EDGE,"E2"),sQuery(id+"F0.wireOp",EDGE,"E3"),sQuery(id+"F0.wireOp",EDGE,"E4"),sQuery(id+"F0.wireOp",EDGE,"E5"),sQuery(id+"F0.wireOp",EDGE,"E6"),sQuery(id+"F0.wireOp",EDGE,"E7"),sQuery(id+"F0.wireOp",EDGE,"E8"),sQuery(id+"F0.wireOp",EDGE,"E9"),sQuery(id+"F0.wireOp",EDGE,"E10.0"),sQuery(id+"F0.wireOp",EDGE,"E10.1"),sQuery(id+"F0.wireOp",EDGE,"E10.2"),sQuery(id+"F0.wireOp",EDGE,"E10.3"),sQuery(id+"F0.wireOp",EDGE,"E10.4"),sQuery(id+"F0.wireOp",EDGE,"E10.5"),sQuery(id+"F0.wireOp",EDGE,"E11"),sQuery(id+"F0.wireOp",EDGE,"E12"),sQuery(id+"F0.wireOp",EDGE,"E13"),sQuery(id+"F0.wireOp",EDGE,"E14"),sQuery(id+"F0.wireOp",EDGE,"E15"),sQuery(id+"F0.wireOp",EDGE,"E16"),sQuery(id+"F0.wireOp",EDGE,"E17"),sQuery(id+"F0.wireOp",EDGE,"E18"),sQuery(id+"F0.wireOp",EDGE,"E19")])],"isStart":true})})}),makeQuery(id+"F22.opExtrude","SWEPT_FACE",FACE,{"disambiguationData":[OSD([sQuery(id+"F21.wireOp",EDGE,"E76")])]})]});}
            var Q31;
            {var subQ0=sQuery(id+"F5.wireOp",EDGE,"E59.5");Q31=makeQuery(id+"F22.boolean.opBoolean","INTERSECT",EDGE,{"derivedFrom":[makeQuery(id+"F6.boolean.opBoolean","SPLIT",FACE,{"disambiguationData":[TD([makeQuery(id+"F6.opExtrude","SWEPT_FACE",FACE,{"disambiguationData":[OSD([subQ0])]})])],"derivedFrom":makeQuery(id+"F2.opChamfer","SPLIT",FACE,{"disambiguationData":[OD(6.0)],"derivedFrom":makeQuery(id+"F1.opExtrude","CAP_FACE",FACE,{"disambiguationData":[OSD([sQuery(id+"F0.wireOp",EDGE,"E0.0"),sQuery(id+"F0.wireOp",EDGE,"E0.1"),sQuery(id+"F0.wireOp",EDGE,"E0.2"),sQuery(id+"F0.wireOp",EDGE,"E0.3"),sQuery(id+"F0.wireOp",EDGE,"E0.4"),sQuery(id+"F0.wireOp",EDGE,"E0.5"),sQuery(id+"F0.wireOp",EDGE,"E1"),sQuery(id+"F0.wireOp",EDGE,"E2"),sQuery(id+"F0.wireOp",EDGE,"E3"),sQuery(id+"F0.wireOp",EDGE,"E4"),sQuery(id+"F0.wireOp",EDGE,"E5"),sQuery(id+"F0.wireOp",EDGE,"E6"),sQuery(id+"F0.wireOp",EDGE,"E7"),sQuery(id+"F0.wireOp",EDGE,"E8"),sQuery(id+"F0.wireOp",EDGE,"E9"),sQuery(id+"F0.wireOp",EDGE,"E10.0"),sQuery(id+"F0.wireOp",EDGE,"E10.1"),sQuery(id+"F0.wireOp",EDGE,"E10.2"),sQuery(id+"F0.wireOp",EDGE,"E10.3"),sQuery(id+"F0.wireOp",EDGE,"E10.4"),sQuery(id+"F0.wireOp",EDGE,"E10.5"),sQuery(id+"F0.wireOp",EDGE,"E11"),sQuery(id+"F0.wireOp",EDGE,"E12"),sQuery(id+"F0.wireOp",EDGE,"E13"),sQuery(id+"F0.wireOp",EDGE,"E14"),sQuery(id+"F0.wireOp",EDGE,"E15"),sQuery(id+"F0.wireOp",EDGE,"E16"),sQuery(id+"F0.wireOp",EDGE,"E17"),sQuery(id+"F0.wireOp",EDGE,"E18"),sQuery(id+"F0.wireOp",EDGE,"E19")])],"isStart":true})})}),makeQuery(id+"F22.opExtrude","SWEPT_FACE",FACE,{"disambiguationData":[OSD([sQuery(id+"F21.wireOp",EDGE,"E77")])]})]});}
            var Q32;
            {var subQ0=sQuery(id+"F5.wireOp",EDGE,"E59.5");Q32=makeQuery(id+"F22.boolean.opBoolean","INTERSECT",EDGE,{"derivedFrom":[makeQuery(id+"F6.boolean.opBoolean","SPLIT",FACE,{"disambiguationData":[TD([makeQuery(id+"F6.opExtrude","SWEPT_FACE",FACE,{"disambiguationData":[OSD([subQ0])]})])],"derivedFrom":makeQuery(id+"F2.opChamfer","SPLIT",FACE,{"disambiguationData":[OD(6.0)],"derivedFrom":makeQuery(id+"F1.opExtrude","CAP_FACE",FACE,{"disambiguationData":[OSD([sQuery(id+"F0.wireOp",EDGE,"E0.0"),sQuery(id+"F0.wireOp",EDGE,"E0.1"),sQuery(id+"F0.wireOp",EDGE,"E0.2"),sQuery(id+"F0.wireOp",EDGE,"E0.3"),sQuery(id+"F0.wireOp",EDGE,"E0.4"),sQuery(id+"F0.wireOp",EDGE,"E0.5"),sQuery(id+"F0.wireOp",EDGE,"E1"),sQuery(id+"F0.wireOp",EDGE,"E2"),sQuery(id+"F0.wireOp",EDGE,"E3"),sQuery(id+"F0.wireOp",EDGE,"E4"),sQuery(id+"F0.wireOp",EDGE,"E5"),sQuery(id+"F0.wireOp",EDGE,"E6"),sQuery(id+"F0.wireOp",EDGE,"E7"),sQuery(id+"F0.wireOp",EDGE,"E8"),sQuery(id+"F0.wireOp",EDGE,"E9"),sQuery(id+"F0.wireOp",EDGE,"E10.0"),sQuery(id+"F0.wireOp",EDGE,"E10.1"),sQuery(id+"F0.wireOp",EDGE,"E10.2"),sQuery(id+"F0.wireOp",EDGE,"E10.3"),sQuery(id+"F0.wireOp",EDGE,"E10.4"),sQuery(id+"F0.wireOp",EDGE,"E10.5"),sQuery(id+"F0.wireOp",EDGE,"E11"),sQuery(id+"F0.wireOp",EDGE,"E12"),sQuery(id+"F0.wireOp",EDGE,"E13"),sQuery(id+"F0.wireOp",EDGE,"E14"),sQuery(id+"F0.wireOp",EDGE,"E15"),sQuery(id+"F0.wireOp",EDGE,"E16"),sQuery(id+"F0.wireOp",EDGE,"E17"),sQuery(id+"F0.wireOp",EDGE,"E18"),sQuery(id+"F0.wireOp",EDGE,"E19")])],"isStart":true})})}),makeQuery(id+"F22.opExtrude","SWEPT_FACE",FACE,{"disambiguationData":[OSD([sQuery(id+"F21.wireOp",EDGE,"E78")])]})]});}
            var Q33;
            {var subQ0=sQuery(id+"F5.wireOp",EDGE,"E59.0");Q33=makeQuery(id+"F18.boolean.opBoolean","INTERSECT",EDGE,{"derivedFrom":[makeQuery(id+"F6.boolean.opBoolean","SPLIT",FACE,{"disambiguationData":[TD([makeQuery(id+"F6.opExtrude","SWEPT_FACE",FACE,{"disambiguationData":[OSD([subQ0])]})])],"derivedFrom":makeQuery(id+"F2.opChamfer","SPLIT",FACE,{"disambiguationData":[OD(6.0)],"derivedFrom":makeQuery(id+"F1.opExtrude","CAP_FACE",FACE,{"disambiguationData":[OSD([sQuery(id+"F0.wireOp",EDGE,"E0.0"),sQuery(id+"F0.wireOp",EDGE,"E0.1"),sQuery(id+"F0.wireOp",EDGE,"E0.2"),sQuery(id+"F0.wireOp",EDGE,"E0.3"),sQuery(id+"F0.wireOp",EDGE,"E0.4"),sQuery(id+"F0.wireOp",EDGE,"E0.5"),sQuery(id+"F0.wireOp",EDGE,"E1"),sQuery(id+"F0.wireOp",EDGE,"E2"),sQuery(id+"F0.wireOp",EDGE,"E3"),sQuery(id+"F0.wireOp",EDGE,"E4"),sQuery(id+"F0.wireOp",EDGE,"E5"),sQuery(id+"F0.wireOp",EDGE,"E6"),sQuery(id+"F0.wireOp",EDGE,"E7"),sQuery(id+"F0.wireOp",EDGE,"E8"),sQuery(id+"F0.wireOp",EDGE,"E9"),sQuery(id+"F0.wireOp",EDGE,"E10.0"),sQuery(id+"F0.wireOp",EDGE,"E10.1"),sQuery(id+"F0.wireOp",EDGE,"E10.2"),sQuery(id+"F0.wireOp",EDGE,"E10.3"),sQuery(id+"F0.wireOp",EDGE,"E10.4"),sQuery(id+"F0.wireOp",EDGE,"E10.5"),sQuery(id+"F0.wireOp",EDGE,"E11"),sQuery(id+"F0.wireOp",EDGE,"E12"),sQuery(id+"F0.wireOp",EDGE,"E13"),sQuery(id+"F0.wireOp",EDGE,"E14"),sQuery(id+"F0.wireOp",EDGE,"E15"),sQuery(id+"F0.wireOp",EDGE,"E16"),sQuery(id+"F0.wireOp",EDGE,"E17"),sQuery(id+"F0.wireOp",EDGE,"E18"),sQuery(id+"F0.wireOp",EDGE,"E19")])],"isStart":true})})}),makeQuery(id+"F18.opExtrude","SWEPT_FACE",FACE,{"disambiguationData":[OSD([sQuery(id+"F17.wireOp",EDGE,"E71")])]})]});}
            var Q34;
            {var subQ0=sQuery(id+"F5.wireOp",EDGE,"E59.0");Q34=makeQuery(id+"F18.boolean.opBoolean","INTERSECT",EDGE,{"derivedFrom":[makeQuery(id+"F6.boolean.opBoolean","SPLIT",FACE,{"disambiguationData":[TD([makeQuery(id+"F6.opExtrude","SWEPT_FACE",FACE,{"disambiguationData":[OSD([subQ0])]})])],"derivedFrom":makeQuery(id+"F2.opChamfer","SPLIT",FACE,{"disambiguationData":[OD(6.0)],"derivedFrom":makeQuery(id+"F1.opExtrude","CAP_FACE",FACE,{"disambiguationData":[OSD([sQuery(id+"F0.wireOp",EDGE,"E0.0"),sQuery(id+"F0.wireOp",EDGE,"E0.1"),sQuery(id+"F0.wireOp",EDGE,"E0.2"),sQuery(id+"F0.wireOp",EDGE,"E0.3"),sQuery(id+"F0.wireOp",EDGE,"E0.4"),sQuery(id+"F0.wireOp",EDGE,"E0.5"),sQuery(id+"F0.wireOp",EDGE,"E1"),sQuery(id+"F0.wireOp",EDGE,"E2"),sQuery(id+"F0.wireOp",EDGE,"E3"),sQuery(id+"F0.wireOp",EDGE,"E4"),sQuery(id+"F0.wireOp",EDGE,"E5"),sQuery(id+"F0.wireOp",EDGE,"E6"),sQuery(id+"F0.wireOp",EDGE,"E7"),sQuery(id+"F0.wireOp",EDGE,"E8"),sQuery(id+"F0.wireOp",EDGE,"E9"),sQuery(id+"F0.wireOp",EDGE,"E10.0"),sQuery(id+"F0.wireOp",EDGE,"E10.1"),sQuery(id+"F0.wireOp",EDGE,"E10.2"),sQuery(id+"F0.wireOp",EDGE,"E10.3"),sQuery(id+"F0.wireOp",EDGE,"E10.4"),sQuery(id+"F0.wireOp",EDGE,"E10.5"),sQuery(id+"F0.wireOp",EDGE,"E11"),sQuery(id+"F0.wireOp",EDGE,"E12"),sQuery(id+"F0.wireOp",EDGE,"E13"),sQuery(id+"F0.wireOp",EDGE,"E14"),sQuery(id+"F0.wireOp",EDGE,"E15"),sQuery(id+"F0.wireOp",EDGE,"E16"),sQuery(id+"F0.wireOp",EDGE,"E17"),sQuery(id+"F0.wireOp",EDGE,"E18"),sQuery(id+"F0.wireOp",EDGE,"E19")])],"isStart":true})})}),makeQuery(id+"F18.opExtrude","SWEPT_FACE",FACE,{"disambiguationData":[OSD([sQuery(id+"F17.wireOp",EDGE,"E70")])]})]});}
            var Q35;
            {var subQ0=sQuery(id+"F5.wireOp",EDGE,"E59.0");Q35=makeQuery(id+"F18.boolean.opBoolean","INTERSECT",EDGE,{"derivedFrom":[makeQuery(id+"F6.boolean.opBoolean","SPLIT",FACE,{"disambiguationData":[TD([makeQuery(id+"F6.opExtrude","SWEPT_FACE",FACE,{"disambiguationData":[OSD([subQ0])]})])],"derivedFrom":makeQuery(id+"F2.opChamfer","SPLIT",FACE,{"disambiguationData":[OD(6.0)],"derivedFrom":makeQuery(id+"F1.opExtrude","CAP_FACE",FACE,{"disambiguationData":[OSD([sQuery(id+"F0.wireOp",EDGE,"E0.0"),sQuery(id+"F0.wireOp",EDGE,"E0.1"),sQuery(id+"F0.wireOp",EDGE,"E0.2"),sQuery(id+"F0.wireOp",EDGE,"E0.3"),sQuery(id+"F0.wireOp",EDGE,"E0.4"),sQuery(id+"F0.wireOp",EDGE,"E0.5"),sQuery(id+"F0.wireOp",EDGE,"E1"),sQuery(id+"F0.wireOp",EDGE,"E2"),sQuery(id+"F0.wireOp",EDGE,"E3"),sQuery(id+"F0.wireOp",EDGE,"E4"),sQuery(id+"F0.wireOp",EDGE,"E5"),sQuery(id+"F0.wireOp",EDGE,"E6"),sQuery(id+"F0.wireOp",EDGE,"E7"),sQuery(id+"F0.wireOp",EDGE,"E8"),sQuery(id+"F0.wireOp",EDGE,"E9"),sQuery(id+"F0.wireOp",EDGE,"E10.0"),sQuery(id+"F0.wireOp",EDGE,"E10.1"),sQuery(id+"F0.wireOp",EDGE,"E10.2"),sQuery(id+"F0.wireOp",EDGE,"E10.3"),sQuery(id+"F0.wireOp",EDGE,"E10.4"),sQuery(id+"F0.wireOp",EDGE,"E10.5"),sQuery(id+"F0.wireOp",EDGE,"E11"),sQuery(id+"F0.wireOp",EDGE,"E12"),sQuery(id+"F0.wireOp",EDGE,"E13"),sQuery(id+"F0.wireOp",EDGE,"E14"),sQuery(id+"F0.wireOp",EDGE,"E15"),sQuery(id+"F0.wireOp",EDGE,"E16"),sQuery(id+"F0.wireOp",EDGE,"E17"),sQuery(id+"F0.wireOp",EDGE,"E18"),sQuery(id+"F0.wireOp",EDGE,"E19")])],"isStart":true})})}),makeQuery(id+"F18.opExtrude","SWEPT_FACE",FACE,{"disambiguationData":[OSD([sQuery(id+"F17.wireOp",EDGE,"E72")])]})]});}
            chamfer(context, id + "F23", {"entities" : qUnion([Q0, Q1, Q2, Q3, Q4, Q5, Q6, Q7, Q8, Q9, Q10, Q11, Q12, Q13, Q14, Q15, Q16, Q17, Q18, Q19, Q20, Q21, Q22, Q23, Q24, Q25, Q26, Q27, Q28, Q29, Q30, Q31, Q32, Q33, Q34, Q35]), "width" : 1 * mm, "tangentPropagation" : true});
        }
    });
